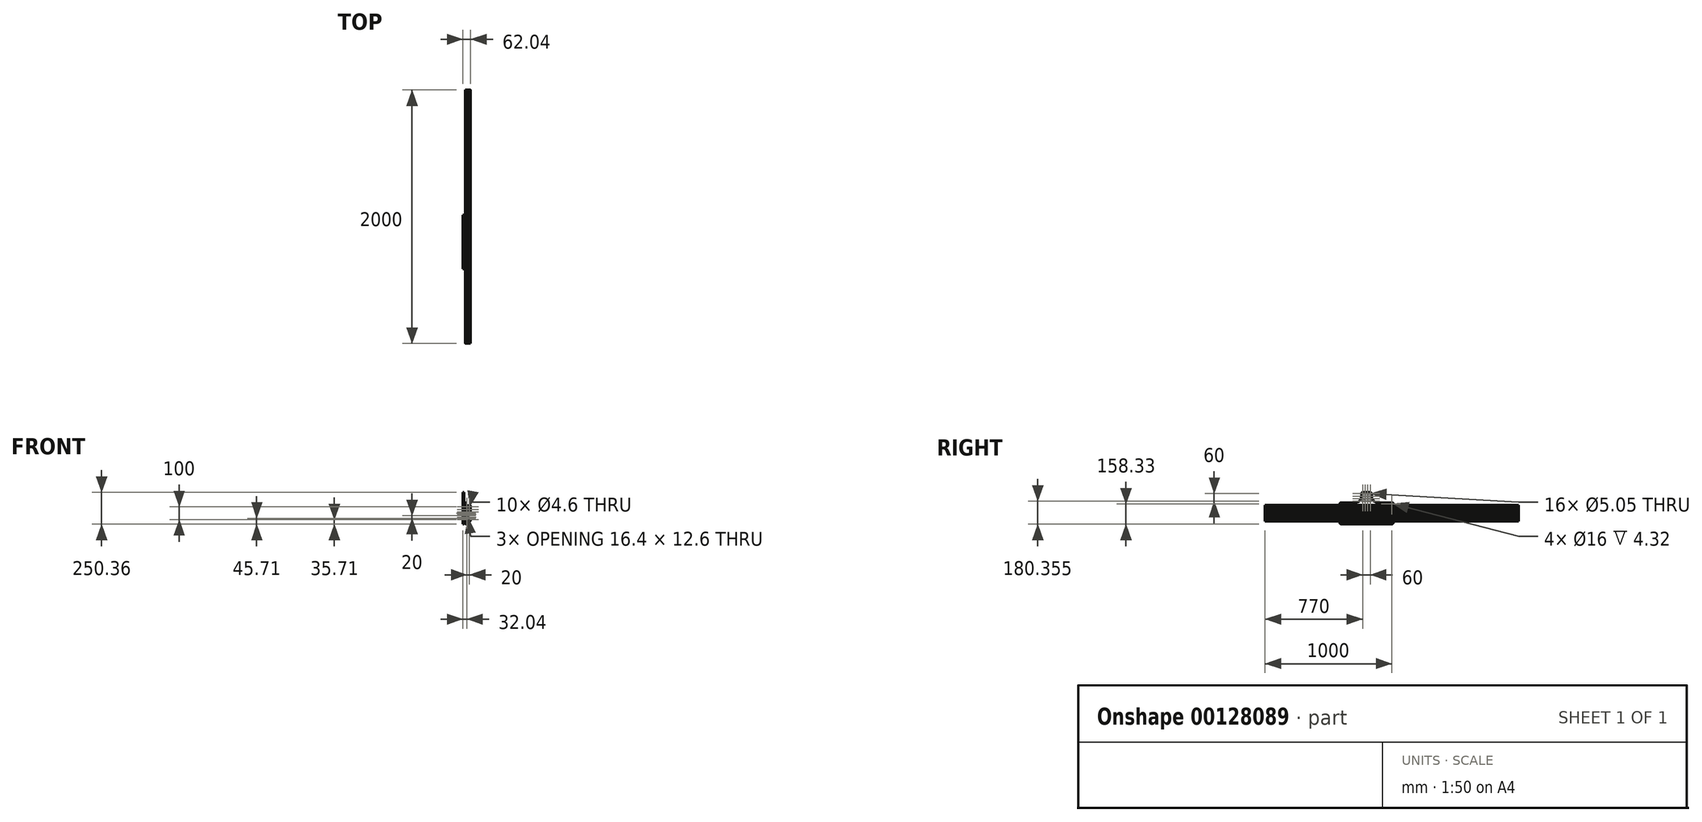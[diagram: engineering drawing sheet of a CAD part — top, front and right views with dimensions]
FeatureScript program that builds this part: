
annotation { "Feature Type Name" : "Feature", "Feature Type Description" : "" }
export const myFeature = defineFeature(function(context is Context, id is Id, definition is map)
    precondition{}
    {
        {
            var Q0;
            Q0=qCreatedBy(makeId("Front.planeOp"),FACE);
            var sketch = newSketch(context, id + "F0", { "sketchPlane" : qUnion([Q0])});
            skLineSegment(sketch, "E0", {"start": v(2.7, -58.2) * mm, "end": v(2.7, -56.24) * mm});
            skLineSegment(sketch, "E1", {"start": v(2.7, -56.24) * mm, "end": v(6.1, -52.84) * mm});
            skLineSegment(sketch, "E2", {"start": v(-1.8, -37.3) * mm, "end": v(-3.79, -37.27) * mm});
            skLineSegment(sketch, "E3", {"start": v(-3.79, -37.27) * mm, "end": v(-7.16, -33.9) * mm});
            skLineSegment(sketch, "E4", {"start": v(-7.16, -33.9) * mm, "end": v(-9.8, -33.9) * mm});
            skLineSegment(sketch, "E5", {"start": v(-9.8, -33.9) * mm, "end": v(-10, -33.7) * mm});
            skLineSegment(sketch, "E6", {"start": v(-10, -33.7) * mm, "end": v(-10.2, -33.9) * mm});
            skLineSegment(sketch, "E7", {"start": v(-10.2, -33.9) * mm, "end": v(-12.84, -33.9) * mm});
            skLineSegment(sketch, "E8", {"start": v(-12.84, -33.9) * mm, "end": v(-16.21, -37.27) * mm});
            skLineSegment(sketch, "E9", {"start": v(-16.21, -37.27) * mm, "end": v(-18.2, -37.3) * mm});
            skLineSegment(sketch, "E10", {"start": v(-18.2, -37.3) * mm, "end": v(-18.2, -40) * mm});
            skLineSegment(sketch, "E11", {"start": v(-18.2, -40) * mm, "end": v(-18.2, -42.7) * mm});
            skLineSegment(sketch, "E12", {"start": v(-18.2, -42.7) * mm, "end": v(-16.21, -42.73) * mm});
            skLineSegment(sketch, "E13", {"start": v(-16.21, -42.73) * mm, "end": v(-12.84, -46.1) * mm});
            skLineSegment(sketch, "E14", {"start": v(-12.84, -46.1) * mm, "end": v(-10.2, -46.1) * mm});
            skLineSegment(sketch, "E15", {"start": v(-10.2, -46.1) * mm, "end": v(-10, -46.3) * mm});
            skLineSegment(sketch, "E16", {"start": v(-10, -46.3) * mm, "end": v(-9.8, -46.1) * mm});
            skLineSegment(sketch, "E17", {"start": v(-9.8, -46.1) * mm, "end": v(-7.16, -46.1) * mm});
            skLineSegment(sketch, "E18", {"start": v(-7.16, -46.1) * mm, "end": v(-1.8, -40.74) * mm});
            skLineSegment(sketch, "E19", {"start": v(-1.8, -40.74) * mm, "end": v(-1.8, -37.3) * mm});
            skLineSegment(sketch, "E20", {"start": v(-6.1, -47.16) * mm, "end": v(-6.1, -49.8) * mm});
            skLineSegment(sketch, "E21", {"start": v(-6.1, -50.2) * mm, "end": v(-6.1, -52.84) * mm});
            skLineSegment(sketch, "E22", {"start": v(-6.1, -52.84) * mm, "end": v(-2.7, -56.24) * mm});
            skLineSegment(sketch, "E23", {"start": v(-2.7, -56.24) * mm, "end": v(-2.7, -58.2) * mm});
            skLineSegment(sketch, "E24", {"start": v(-2.7, -58.2) * mm, "end": v(0, -58.2) * mm});
            skLineSegment(sketch, "E25", {"start": v(0, -58.2) * mm, "end": v(2.7, -58.2) * mm});
            skCircle(sketch, "E26", {"center": v(-10, -50) * mm, "radius": 2.3 * mm});
            skCircle(sketch, "E27", {"center": v(10, -50) * mm, "radius": 2.3 * mm});
            skLineSegment(sketch, "E28", {"start": v(-6.1, -47.16) * mm, "end": v(-0.74, -41.8) * mm});
            skLineSegment(sketch, "E29", {"start": v(-0.74, -41.8) * mm, "end": v(2.7, -41.8) * mm});
            skLineSegment(sketch, "E30", {"start": v(2.7, -41.8) * mm, "end": v(2.7, -43.76) * mm});
            skLineSegment(sketch, "E31", {"start": v(2.7, -43.76) * mm, "end": v(6.1, -47.16) * mm});
            skLineSegment(sketch, "E32", {"start": v(6.1, -47.16) * mm, "end": v(6.1, -49.8) * mm});
            skLineSegment(sketch, "E33", {"start": v(6.1, -49.8) * mm, "end": v(6.3, -50) * mm});
            skLineSegment(sketch, "E34", {"start": v(6.3, -50) * mm, "end": v(6.1, -50.2) * mm});
            skLineSegment(sketch, "E35", {"start": v(6.1, -50.2) * mm, "end": v(6.1, -52.84) * mm});
            skLineSegment(sketch, "E36", {"start": v(-6.1, -50.2) * mm, "end": v(-6.3, -50) * mm});
            skLineSegment(sketch, "E37", {"start": v(-6.3, -50) * mm, "end": v(-6.1, -49.8) * mm});
            skCircle(sketch, "E38", {"center": v(-10, -30) * mm, "radius": 2.3 * mm});
            skLineSegment(sketch, "E39", {"start": v(-3.79, -17.27) * mm, "end": v(-1.8, -17.3) * mm});
            skLineSegment(sketch, "E40", {"start": v(-1.8, -17.3) * mm, "end": v(-1.8, -22.7) * mm});
            skLineSegment(sketch, "E41", {"start": v(-1.8, -22.7) * mm, "end": v(-3.79, -22.73) * mm});
            skLineSegment(sketch, "E42", {"start": v(-3.79, -22.73) * mm, "end": v(-7.16, -26.1) * mm});
            skLineSegment(sketch, "E43", {"start": v(-7.16, -26.1) * mm, "end": v(-9.8, -26.1) * mm});
            skLineSegment(sketch, "E44", {"start": v(-9.8, -26.1) * mm, "end": v(-10, -26.3) * mm});
            skLineSegment(sketch, "E45", {"start": v(-10, -26.3) * mm, "end": v(-10.2, -26.1) * mm});
            skLineSegment(sketch, "E46", {"start": v(-10.2, -26.1) * mm, "end": v(-12.84, -26.1) * mm});
            skLineSegment(sketch, "E47", {"start": v(-12.84, -26.1) * mm, "end": v(-16.21, -22.73) * mm});
            skLineSegment(sketch, "E48", {"start": v(-16.21, -22.73) * mm, "end": v(-18.2, -22.7) * mm});
            skLineSegment(sketch, "E49", {"start": v(-18.2, -22.7) * mm, "end": v(-18.2, -20) * mm});
            skLineSegment(sketch, "E50", {"start": v(-18.2, -20) * mm, "end": v(-18.2, -17.3) * mm});
            skLineSegment(sketch, "E51", {"start": v(-18.2, -17.3) * mm, "end": v(-16.21, -17.27) * mm});
            skLineSegment(sketch, "E52", {"start": v(-16.21, -17.27) * mm, "end": v(-12.84, -13.9) * mm});
            skLineSegment(sketch, "E53", {"start": v(-12.84, -13.9) * mm, "end": v(-10.2, -13.9) * mm});
            skLineSegment(sketch, "E54", {"start": v(-10.2, -13.9) * mm, "end": v(-10, -13.7) * mm});
            skLineSegment(sketch, "E55", {"start": v(-10, -13.7) * mm, "end": v(-9.8, -13.9) * mm});
            skLineSegment(sketch, "E56", {"start": v(-9.8, -13.9) * mm, "end": v(-7.16, -13.9) * mm});
            skLineSegment(sketch, "E57", {"start": v(-7.16, -13.9) * mm, "end": v(-3.79, -17.27) * mm});
            skLineSegment(sketch, "E58", {"start": v(-6.1, -32.84) * mm, "end": v(-6.1, -30.2) * mm});
            skLineSegment(sketch, "E59", {"start": v(-6.1, -30.2) * mm, "end": v(-6.3, -30) * mm});
            skLineSegment(sketch, "E60", {"start": v(-6.3, -30) * mm, "end": v(-6.1, -29.8) * mm});
            skLineSegment(sketch, "E61", {"start": v(-6.1, -29.8) * mm, "end": v(-6.1, -27.16) * mm});
            skLineSegment(sketch, "E62", {"start": v(-6.1, -27.16) * mm, "end": v(-3.44, -24.5) * mm});
            skLineSegment(sketch, "E63", {"start": v(-3.44, -24.5) * mm, "end": v(-1.8, -24.5) * mm});
            skLineSegment(sketch, "E64", {"start": v(-1.8, -24.5) * mm, "end": v(-1.8, -26.61) * mm});
            skLineSegment(sketch, "E65", {"start": v(-1.8, -26.61) * mm, "end": v(-1.2, -26.61) * mm});
            skLineSegment(sketch, "E66", {"start": v(-1.2, -26.61) * mm, "end": v(-0.18, -25.6) * mm});
            skArc(sketch, "E67", {"start": v(-0.18, -25.6) * mm, "mid": v(-0.05, -25.4) * mm, "end": v(0, -25.17) * mm});
            skLineSegment(sketch, "E68", {"start": v(0, -25.17) * mm, "end": v(0, -20.2) * mm});
            skLineSegment(sketch, "E69", {"start": v(0, -20.2) * mm, "end": v(-0.2, -20) * mm});
            skLineSegment(sketch, "E70", {"start": v(-0.2, -20) * mm, "end": v(0, -19.8) * mm});
            skLineSegment(sketch, "E71", {"start": v(0, -19.8) * mm, "end": v(0, -14.83) * mm});
            skArc(sketch, "E72", {"start": v(0, -14.83) * mm, "mid": v(-0.05, -14.6) * mm, "end": v(-0.18, -14.4) * mm});
            skLineSegment(sketch, "E73", {"start": v(-0.18, -14.4) * mm, "end": v(-1.2, -13.39) * mm});
            skLineSegment(sketch, "E74", {"start": v(-1.2, -13.39) * mm, "end": v(-1.8, -13.39) * mm});
            skLineSegment(sketch, "E75", {"start": v(-1.8, -13.39) * mm, "end": v(-1.8, -15.5) * mm});
            skLineSegment(sketch, "E76", {"start": v(-1.8, -15.5) * mm, "end": v(-3.44, -15.5) * mm});
            skLineSegment(sketch, "E77", {"start": v(-3.44, -15.5) * mm, "end": v(-6.1, -12.84) * mm});
            skLineSegment(sketch, "E78", {"start": v(-6.1, -12.84) * mm, "end": v(-6.1, -10.2) * mm});
            skLineSegment(sketch, "E79", {"start": v(-6.1, -10.2) * mm, "end": v(-6.3, -10) * mm});
            skLineSegment(sketch, "E80", {"start": v(-6.3, -10) * mm, "end": v(-6.1, -9.8) * mm});
            skLineSegment(sketch, "E81", {"start": v(-6.1, -9.8) * mm, "end": v(-6.1, -7.16) * mm});
            skLineSegment(sketch, "E82", {"start": v(-6.1, -7.16) * mm, "end": v(-3.44, -4.5) * mm});
            skLineSegment(sketch, "E83", {"start": v(-3.44, -4.5) * mm, "end": v(-1.8, -4.5) * mm});
            skLineSegment(sketch, "E84", {"start": v(-1.8, -4.5) * mm, "end": v(-1.8, -6.61) * mm});
            skLineSegment(sketch, "E85", {"start": v(-1.8, -6.61) * mm, "end": v(-1.2, -6.61) * mm});
            skLineSegment(sketch, "E86", {"start": v(-1.2, -6.61) * mm, "end": v(-0.18, -5.6) * mm});
            skArc(sketch, "E87", {"start": v(-0.18, -5.6) * mm, "mid": v(-0.05, -5.4) * mm, "end": v(0, -5.17) * mm});
            skLineSegment(sketch, "E88", {"start": v(0, -5.17) * mm, "end": v(0, 0) * mm});
            skLineSegment(sketch, "E89", {"start": v(0, 0) * mm, "end": v(5.17, 0) * mm});
            skArc(sketch, "E90", {"start": v(5.17, 0) * mm, "mid": v(5.4, 0.05) * mm, "end": v(5.6, 0.18) * mm});
            skLineSegment(sketch, "E91", {"start": v(5.6, 0.18) * mm, "end": v(6.61, 1.2) * mm});
            skLineSegment(sketch, "E92", {"start": v(6.61, 1.2) * mm, "end": v(6.61, 1.8) * mm});
            skLineSegment(sketch, "E93", {"start": v(6.61, 1.8) * mm, "end": v(4.5, 1.8) * mm});
            skLineSegment(sketch, "E94", {"start": v(4.5, 1.8) * mm, "end": v(4.5, 3.44) * mm});
            skLineSegment(sketch, "E95", {"start": v(4.5, 3.44) * mm, "end": v(7.16, 6.1) * mm});
            skLineSegment(sketch, "E96", {"start": v(7.16, 6.1) * mm, "end": v(9.8, 6.1) * mm});
            skLineSegment(sketch, "E97", {"start": v(9.8, 6.1) * mm, "end": v(10, 6.3) * mm});
            skLineSegment(sketch, "E98", {"start": v(10, 6.3) * mm, "end": v(10.2, 6.1) * mm});
            skLineSegment(sketch, "E99", {"start": v(10.2, 6.1) * mm, "end": v(12.84, 6.1) * mm});
            skLineSegment(sketch, "E100", {"start": v(12.84, 6.1) * mm, "end": v(15.5, 3.44) * mm});
            skLineSegment(sketch, "E101", {"start": v(15.5, 3.44) * mm, "end": v(15.5, 1.8) * mm});
            skLineSegment(sketch, "E102", {"start": v(15.5, 1.8) * mm, "end": v(13.39, 1.8) * mm});
            skLineSegment(sketch, "E103", {"start": v(13.39, 1.8) * mm, "end": v(13.39, 1.2) * mm});
            skLineSegment(sketch, "E104", {"start": v(13.39, 1.2) * mm, "end": v(14.4, 0.18) * mm});
            skArc(sketch, "E105", {"start": v(14.4, 0.18) * mm, "mid": v(14.6, 0.05) * mm, "end": v(14.83, 0) * mm});
            skLineSegment(sketch, "E106", {"start": v(14.83, 0) * mm, "end": v(18.5, 0) * mm});
            skArc(sketch, "E107", {"start": v(18.5, 0) * mm, "mid": v(19.56, 0.44) * mm, "end": v(20, 1.5) * mm});
            skLineSegment(sketch, "E108", {"start": v(20, 1.5) * mm, "end": v(20, 5.17) * mm});
            skArc(sketch, "E109", {"start": v(20, 5.17) * mm, "mid": v(19.95, 5.4) * mm, "end": v(19.82, 5.6) * mm});
            skLineSegment(sketch, "E110", {"start": v(19.82, 5.6) * mm, "end": v(18.8, 6.61) * mm});
            skLineSegment(sketch, "E111", {"start": v(18.8, 6.61) * mm, "end": v(18.2, 6.61) * mm});
            skLineSegment(sketch, "E112", {"start": v(18.2, 6.61) * mm, "end": v(18.2, 4.5) * mm});
            skLineSegment(sketch, "E113", {"start": v(18.2, 4.5) * mm, "end": v(16.56, 4.5) * mm});
            skLineSegment(sketch, "E114", {"start": v(16.56, 4.5) * mm, "end": v(13.9, 7.16) * mm});
            skLineSegment(sketch, "E115", {"start": v(13.9, 7.16) * mm, "end": v(13.9, 9.8) * mm});
            skLineSegment(sketch, "E116", {"start": v(13.9, 9.8) * mm, "end": v(13.7, 10) * mm});
            skLineSegment(sketch, "E117", {"start": v(13.7, 10) * mm, "end": v(13.9, 10.2) * mm});
            skLineSegment(sketch, "E118", {"start": v(13.9, 10.2) * mm, "end": v(13.9, 12.84) * mm});
            skLineSegment(sketch, "E119", {"start": v(13.9, 12.84) * mm, "end": v(16.56, 15.5) * mm});
            skLineSegment(sketch, "E120", {"start": v(16.56, 15.5) * mm, "end": v(18.2, 15.5) * mm});
            skLineSegment(sketch, "E121", {"start": v(18.2, 15.5) * mm, "end": v(18.2, 13.39) * mm});
            skLineSegment(sketch, "E122", {"start": v(18.2, 13.39) * mm, "end": v(18.8, 13.39) * mm});
            skLineSegment(sketch, "E123", {"start": v(18.8, 13.39) * mm, "end": v(19.82, 14.4) * mm});
            skArc(sketch, "E124", {"start": v(19.82, 14.4) * mm, "mid": v(19.95, 14.6) * mm, "end": v(20, 14.83) * mm});
            skLineSegment(sketch, "E125", {"start": v(20, 14.83) * mm, "end": v(20, 18.5) * mm});
            skArc(sketch, "E126", {"start": v(20, 18.5) * mm, "mid": v(19.56, 19.56) * mm, "end": v(18.5, 20) * mm});
            skLineSegment(sketch, "E127", {"start": v(18.5, 20) * mm, "end": v(14.83, 20) * mm});
            skArc(sketch, "E128", {"start": v(14.83, 20) * mm, "mid": v(14.6, 19.95) * mm, "end": v(14.4, 19.82) * mm});
            skLineSegment(sketch, "E129", {"start": v(14.4, 19.82) * mm, "end": v(13.39, 18.8) * mm});
            skLineSegment(sketch, "E130", {"start": v(13.39, 18.8) * mm, "end": v(13.39, 18.2) * mm});
            skLineSegment(sketch, "E131", {"start": v(13.39, 18.2) * mm, "end": v(15.5, 18.2) * mm});
            skLineSegment(sketch, "E132", {"start": v(15.5, 18.2) * mm, "end": v(15.5, 16.56) * mm});
            skLineSegment(sketch, "E133", {"start": v(15.5, 16.56) * mm, "end": v(12.84, 13.9) * mm});
            skLineSegment(sketch, "E134", {"start": v(12.84, 13.9) * mm, "end": v(10.2, 13.9) * mm});
            skLineSegment(sketch, "E135", {"start": v(10.2, 13.9) * mm, "end": v(10, 13.7) * mm});
            skLineSegment(sketch, "E136", {"start": v(10, 13.7) * mm, "end": v(9.8, 13.9) * mm});
            skLineSegment(sketch, "E137", {"start": v(9.8, 13.9) * mm, "end": v(7.16, 13.9) * mm});
            skLineSegment(sketch, "E138", {"start": v(7.16, 13.9) * mm, "end": v(4.5, 16.56) * mm});
            skLineSegment(sketch, "E139", {"start": v(4.5, 16.56) * mm, "end": v(4.5, 18.2) * mm});
            skLineSegment(sketch, "E140", {"start": v(4.5, 18.2) * mm, "end": v(6.61, 18.2) * mm});
            skLineSegment(sketch, "E141", {"start": v(6.61, 18.2) * mm, "end": v(6.61, 18.8) * mm});
            skLineSegment(sketch, "E142", {"start": v(6.61, 18.8) * mm, "end": v(5.6, 19.82) * mm});
            skArc(sketch, "E143", {"start": v(5.6, 19.82) * mm, "mid": v(5.4, 19.95) * mm, "end": v(5.17, 20) * mm});
            skLineSegment(sketch, "E144", {"start": v(5.17, 20) * mm, "end": v(0.2, 20) * mm});
            skLineSegment(sketch, "E145", {"start": v(0.2, 20) * mm, "end": v(0, 19.8) * mm});
            skLineSegment(sketch, "E146", {"start": v(0, 19.8) * mm, "end": v(-0.2, 20) * mm});
            skLineSegment(sketch, "E147", {"start": v(-0.2, 20) * mm, "end": v(-5.17, 20) * mm});
            skArc(sketch, "E148", {"start": v(-5.17, 20) * mm, "mid": v(-5.4, 19.95) * mm, "end": v(-5.6, 19.82) * mm});
            skLineSegment(sketch, "E149", {"start": v(-5.6, 19.82) * mm, "end": v(-6.61, 18.8) * mm});
            skLineSegment(sketch, "E150", {"start": v(-6.61, 18.8) * mm, "end": v(-6.61, 18.2) * mm});
            skLineSegment(sketch, "E151", {"start": v(-6.61, 18.2) * mm, "end": v(-4.5, 18.2) * mm});
            skLineSegment(sketch, "E152", {"start": v(-4.5, 18.2) * mm, "end": v(-4.5, 16.56) * mm});
            skLineSegment(sketch, "E153", {"start": v(-4.5, 16.56) * mm, "end": v(-7.16, 13.9) * mm});
            skLineSegment(sketch, "E154", {"start": v(-7.16, 13.9) * mm, "end": v(-9.8, 13.9) * mm});
            skLineSegment(sketch, "E155", {"start": v(-9.8, 13.9) * mm, "end": v(-10, 13.7) * mm});
            skLineSegment(sketch, "E156", {"start": v(-10, 13.7) * mm, "end": v(-10.2, 13.9) * mm});
            skLineSegment(sketch, "E157", {"start": v(-10.2, 13.9) * mm, "end": v(-12.84, 13.9) * mm});
            skLineSegment(sketch, "E158", {"start": v(-12.84, 13.9) * mm, "end": v(-15.5, 16.56) * mm});
            skLineSegment(sketch, "E159", {"start": v(-15.5, 16.56) * mm, "end": v(-15.5, 18.2) * mm});
            skLineSegment(sketch, "E160", {"start": v(-15.5, 18.2) * mm, "end": v(-13.39, 18.2) * mm});
            skLineSegment(sketch, "E161", {"start": v(-13.39, 18.2) * mm, "end": v(-13.39, 18.8) * mm});
            skLineSegment(sketch, "E162", {"start": v(-13.39, 18.8) * mm, "end": v(-14.4, 19.82) * mm});
            skArc(sketch, "E163", {"start": v(-14.4, 19.82) * mm, "mid": v(-14.6, 19.95) * mm, "end": v(-14.83, 20) * mm});
            skLineSegment(sketch, "E164", {"start": v(-14.83, 20) * mm, "end": v(-18.5, 20) * mm});
            skArc(sketch, "E165", {"start": v(-18.5, 20) * mm, "mid": v(-19.56, 19.56) * mm, "end": v(-20, 18.5) * mm});
            skLineSegment(sketch, "E166", {"start": v(-20, 18.5) * mm, "end": v(-20, 14.83) * mm});
            skArc(sketch, "E167", {"start": v(-20, 14.83) * mm, "mid": v(-19.95, 14.6) * mm, "end": v(-19.82, 14.4) * mm});
            skLineSegment(sketch, "E168", {"start": v(-19.82, 14.4) * mm, "end": v(-18.8, 13.39) * mm});
            skLineSegment(sketch, "E169", {"start": v(-18.8, 13.39) * mm, "end": v(-18.2, 13.39) * mm});
            skLineSegment(sketch, "E170", {"start": v(-18.2, 13.39) * mm, "end": v(-18.2, 15.5) * mm});
            skLineSegment(sketch, "E171", {"start": v(-18.2, 15.5) * mm, "end": v(-16.56, 15.5) * mm});
            skLineSegment(sketch, "E172", {"start": v(-16.56, 15.5) * mm, "end": v(-13.9, 12.84) * mm});
            skLineSegment(sketch, "E173", {"start": v(-13.9, 12.84) * mm, "end": v(-13.9, 10.2) * mm});
            skLineSegment(sketch, "E174", {"start": v(-13.9, 10.2) * mm, "end": v(-13.7, 10) * mm});
            skLineSegment(sketch, "E175", {"start": v(-13.7, 10) * mm, "end": v(-13.9, 9.8) * mm});
            skLineSegment(sketch, "E176", {"start": v(-13.9, 9.8) * mm, "end": v(-13.9, 7.16) * mm});
            skLineSegment(sketch, "E177", {"start": v(-13.9, 7.16) * mm, "end": v(-16.56, 4.5) * mm});
            skLineSegment(sketch, "E178", {"start": v(-16.56, 4.5) * mm, "end": v(-18.2, 4.5) * mm});
            skLineSegment(sketch, "E179", {"start": v(-18.2, 4.5) * mm, "end": v(-18.2, 6.61) * mm});
            skLineSegment(sketch, "E180", {"start": v(-18.2, 6.61) * mm, "end": v(-18.8, 6.61) * mm});
            skLineSegment(sketch, "E181", {"start": v(-18.8, 6.61) * mm, "end": v(-19.82, 5.6) * mm});
            skArc(sketch, "E182", {"start": v(-19.82, 5.6) * mm, "mid": v(-19.95, 5.4) * mm, "end": v(-20, 5.17) * mm});
            skLineSegment(sketch, "E183", {"start": v(-20, 5.17) * mm, "end": v(-20, 0.2) * mm});
            skLineSegment(sketch, "E184", {"start": v(-20, 0.2) * mm, "end": v(-19.8, 0) * mm});
            skLineSegment(sketch, "E185", {"start": v(-19.8, 0) * mm, "end": v(-20, -0.2) * mm});
            skLineSegment(sketch, "E186", {"start": v(-20, -0.2) * mm, "end": v(-20, -5.17) * mm});
            skArc(sketch, "E187", {"start": v(-20, -5.17) * mm, "mid": v(-19.95, -5.4) * mm, "end": v(-19.82, -5.6) * mm});
            skLineSegment(sketch, "E188", {"start": v(-19.82, -5.6) * mm, "end": v(-18.8, -6.61) * mm});
            skLineSegment(sketch, "E189", {"start": v(-18.8, -6.61) * mm, "end": v(-18.2, -6.61) * mm});
            skLineSegment(sketch, "E190", {"start": v(-18.2, -6.61) * mm, "end": v(-18.2, -4.5) * mm});
            skLineSegment(sketch, "E191", {"start": v(-18.2, -4.5) * mm, "end": v(-16.56, -4.5) * mm});
            skLineSegment(sketch, "E192", {"start": v(-16.56, -4.5) * mm, "end": v(-13.9, -7.16) * mm});
            skLineSegment(sketch, "E193", {"start": v(-13.9, -7.16) * mm, "end": v(-13.9, -9.8) * mm});
            skLineSegment(sketch, "E194", {"start": v(-13.9, -9.8) * mm, "end": v(-13.7, -10) * mm});
            skLineSegment(sketch, "E195", {"start": v(-13.7, -10) * mm, "end": v(-13.9, -10.2) * mm});
            skLineSegment(sketch, "E196", {"start": v(-13.9, -10.2) * mm, "end": v(-13.9, -12.84) * mm});
            skLineSegment(sketch, "E197", {"start": v(-13.9, -12.84) * mm, "end": v(-16.56, -15.5) * mm});
            skLineSegment(sketch, "E198", {"start": v(-16.56, -15.5) * mm, "end": v(-18.2, -15.5) * mm});
            skLineSegment(sketch, "E199", {"start": v(-18.2, -15.5) * mm, "end": v(-18.2, -13.39) * mm});
            skLineSegment(sketch, "E200", {"start": v(-18.2, -13.39) * mm, "end": v(-18.8, -13.39) * mm});
            skLineSegment(sketch, "E201", {"start": v(-18.8, -13.39) * mm, "end": v(-19.82, -14.4) * mm});
            skArc(sketch, "E202", {"start": v(-19.82, -14.4) * mm, "mid": v(-19.95, -14.6) * mm, "end": v(-20, -14.83) * mm});
            skLineSegment(sketch, "E203", {"start": v(-20, -14.83) * mm, "end": v(-20, -19.8) * mm});
            skLineSegment(sketch, "E204", {"start": v(-20, -19.8) * mm, "end": v(-19.8, -20) * mm});
            skLineSegment(sketch, "E205", {"start": v(-19.8, -20) * mm, "end": v(-20, -20.2) * mm});
            skLineSegment(sketch, "E206", {"start": v(-20, -20.2) * mm, "end": v(-20, -25.17) * mm});
            skArc(sketch, "E207", {"start": v(-20, -25.17) * mm, "mid": v(-19.95, -25.4) * mm, "end": v(-19.82, -25.6) * mm});
            skLineSegment(sketch, "E208", {"start": v(-19.82, -25.6) * mm, "end": v(-18.8, -26.61) * mm});
            skLineSegment(sketch, "E209", {"start": v(-18.8, -26.61) * mm, "end": v(-18.2, -26.61) * mm});
            skLineSegment(sketch, "E210", {"start": v(-18.2, -26.61) * mm, "end": v(-18.2, -24.5) * mm});
            skLineSegment(sketch, "E211", {"start": v(-18.2, -24.5) * mm, "end": v(-16.56, -24.5) * mm});
            skLineSegment(sketch, "E212", {"start": v(-16.56, -24.5) * mm, "end": v(-13.9, -27.16) * mm});
            skLineSegment(sketch, "E213", {"start": v(-13.9, -27.16) * mm, "end": v(-13.9, -29.8) * mm});
            skLineSegment(sketch, "E214", {"start": v(-13.9, -29.8) * mm, "end": v(-13.7, -30) * mm});
            skLineSegment(sketch, "E215", {"start": v(-13.7, -30) * mm, "end": v(-13.9, -30.2) * mm});
            skLineSegment(sketch, "E216", {"start": v(-13.9, -30.2) * mm, "end": v(-13.9, -32.84) * mm});
            skLineSegment(sketch, "E217", {"start": v(-13.9, -32.84) * mm, "end": v(-16.56, -35.5) * mm});
            skLineSegment(sketch, "E218", {"start": v(-16.56, -35.5) * mm, "end": v(-18.2, -35.5) * mm});
            skLineSegment(sketch, "E219", {"start": v(-18.2, -35.5) * mm, "end": v(-18.2, -33.39) * mm});
            skLineSegment(sketch, "E220", {"start": v(-18.2, -33.39) * mm, "end": v(-18.8, -33.39) * mm});
            skLineSegment(sketch, "E221", {"start": v(-18.8, -33.39) * mm, "end": v(-19.82, -34.4) * mm});
            skArc(sketch, "E222", {"start": v(-19.82, -34.4) * mm, "mid": v(-19.95, -34.6) * mm, "end": v(-20, -34.83) * mm});
            skLineSegment(sketch, "E223", {"start": v(-20, -34.83) * mm, "end": v(-20, -39.8) * mm});
            skLineSegment(sketch, "E224", {"start": v(-20, -39.8) * mm, "end": v(-19.8, -40) * mm});
            skLineSegment(sketch, "E225", {"start": v(-19.8, -40) * mm, "end": v(-20, -40.2) * mm});
            skLineSegment(sketch, "E226", {"start": v(-20, -40.2) * mm, "end": v(-20, -45.17) * mm});
            skArc(sketch, "E227", {"start": v(-20, -45.17) * mm, "mid": v(-19.95, -45.4) * mm, "end": v(-19.82, -45.6) * mm});
            skLineSegment(sketch, "E228", {"start": v(-19.82, -45.6) * mm, "end": v(-18.8, -46.61) * mm});
            skLineSegment(sketch, "E229", {"start": v(-18.8, -46.61) * mm, "end": v(-18.2, -46.61) * mm});
            skLineSegment(sketch, "E230", {"start": v(-18.2, -46.61) * mm, "end": v(-18.2, -44.5) * mm});
            skLineSegment(sketch, "E231", {"start": v(-18.2, -44.5) * mm, "end": v(-16.56, -44.5) * mm});
            skLineSegment(sketch, "E232", {"start": v(-16.56, -44.5) * mm, "end": v(-13.9, -47.16) * mm});
            skLineSegment(sketch, "E233", {"start": v(-13.9, -47.16) * mm, "end": v(-13.9, -49.8) * mm});
            skLineSegment(sketch, "E234", {"start": v(-13.9, -49.8) * mm, "end": v(-13.7, -50) * mm});
            skLineSegment(sketch, "E235", {"start": v(-13.7, -50) * mm, "end": v(-13.9, -50.2) * mm});
            skLineSegment(sketch, "E236", {"start": v(-13.9, -50.2) * mm, "end": v(-13.9, -52.84) * mm});
            skLineSegment(sketch, "E237", {"start": v(-13.9, -52.84) * mm, "end": v(-16.56, -55.5) * mm});
            skLineSegment(sketch, "E238", {"start": v(-16.56, -55.5) * mm, "end": v(-18.2, -55.5) * mm});
            skLineSegment(sketch, "E239", {"start": v(-18.2, -55.5) * mm, "end": v(-18.2, -53.39) * mm});
            skLineSegment(sketch, "E240", {"start": v(-18.2, -53.39) * mm, "end": v(-18.8, -53.39) * mm});
            skLineSegment(sketch, "E241", {"start": v(-18.8, -53.39) * mm, "end": v(-19.82, -54.4) * mm});
            skArc(sketch, "E242", {"start": v(-19.82, -54.4) * mm, "mid": v(-19.95, -54.6) * mm, "end": v(-20, -54.83) * mm});
            skLineSegment(sketch, "E243", {"start": v(-20, -54.83) * mm, "end": v(-20, -58.5) * mm});
            skArc(sketch, "E244", {"start": v(-20, -58.5) * mm, "mid": v(-19.56, -59.56) * mm, "end": v(-18.5, -60) * mm});
            skLineSegment(sketch, "E245", {"start": v(-18.5, -60) * mm, "end": v(-14.83, -60) * mm});
            skArc(sketch, "E246", {"start": v(-14.83, -60) * mm, "mid": v(-14.6, -59.95) * mm, "end": v(-14.4, -59.82) * mm});
            skLineSegment(sketch, "E247", {"start": v(-14.4, -59.82) * mm, "end": v(-13.39, -58.8) * mm});
            skLineSegment(sketch, "E248", {"start": v(-13.39, -58.8) * mm, "end": v(-13.39, -58.2) * mm});
            skLineSegment(sketch, "E249", {"start": v(-13.39, -58.2) * mm, "end": v(-15.5, -58.2) * mm});
            skLineSegment(sketch, "E250", {"start": v(-15.5, -58.2) * mm, "end": v(-15.5, -56.56) * mm});
            skLineSegment(sketch, "E251", {"start": v(-15.5, -56.56) * mm, "end": v(-12.84, -53.9) * mm});
            skLineSegment(sketch, "E252", {"start": v(-12.84, -53.9) * mm, "end": v(-10.2, -53.9) * mm});
            skLineSegment(sketch, "E253", {"start": v(-10.2, -53.9) * mm, "end": v(-10, -53.7) * mm});
            skLineSegment(sketch, "E254", {"start": v(-10, -53.7) * mm, "end": v(-9.8, -53.9) * mm});
            skLineSegment(sketch, "E255", {"start": v(-9.8, -53.9) * mm, "end": v(-7.16, -53.9) * mm});
            skLineSegment(sketch, "E256", {"start": v(-7.16, -53.9) * mm, "end": v(-4.5, -56.56) * mm});
            skLineSegment(sketch, "E257", {"start": v(-4.5, -56.56) * mm, "end": v(-4.5, -58.2) * mm});
            skLineSegment(sketch, "E258", {"start": v(-4.5, -58.2) * mm, "end": v(-6.61, -58.2) * mm});
            skLineSegment(sketch, "E259", {"start": v(-6.61, -58.2) * mm, "end": v(-6.61, -58.8) * mm});
            skLineSegment(sketch, "E260", {"start": v(-6.61, -58.8) * mm, "end": v(-5.6, -59.82) * mm});
            skArc(sketch, "E261", {"start": v(-5.6, -59.82) * mm, "mid": v(-5.4, -59.95) * mm, "end": v(-5.17, -60) * mm});
            skLineSegment(sketch, "E262", {"start": v(-5.17, -60) * mm, "end": v(-0.2, -60) * mm});
            skLineSegment(sketch, "E263", {"start": v(-0.2, -60) * mm, "end": v(0, -59.8) * mm});
            skLineSegment(sketch, "E264", {"start": v(0, -59.8) * mm, "end": v(0.2, -60) * mm});
            skLineSegment(sketch, "E265", {"start": v(0.2, -60) * mm, "end": v(5.17, -60) * mm});
            skArc(sketch, "E266", {"start": v(5.17, -60) * mm, "mid": v(5.4, -59.95) * mm, "end": v(5.6, -59.82) * mm});
            skLineSegment(sketch, "E267", {"start": v(5.6, -59.82) * mm, "end": v(6.61, -58.8) * mm});
            skLineSegment(sketch, "E268", {"start": v(6.61, -58.8) * mm, "end": v(6.61, -58.2) * mm});
            skLineSegment(sketch, "E269", {"start": v(6.61, -58.2) * mm, "end": v(4.5, -58.2) * mm});
            skLineSegment(sketch, "E270", {"start": v(4.5, -58.2) * mm, "end": v(4.5, -56.56) * mm});
            skLineSegment(sketch, "E271", {"start": v(4.5, -56.56) * mm, "end": v(7.16, -53.9) * mm});
            skLineSegment(sketch, "E272", {"start": v(7.16, -53.9) * mm, "end": v(9.8, -53.9) * mm});
            skLineSegment(sketch, "E273", {"start": v(9.8, -53.9) * mm, "end": v(10, -53.7) * mm});
            skLineSegment(sketch, "E274", {"start": v(10, -53.7) * mm, "end": v(10.2, -53.9) * mm});
            skLineSegment(sketch, "E275", {"start": v(10.2, -53.9) * mm, "end": v(12.84, -53.9) * mm});
            skLineSegment(sketch, "E276", {"start": v(12.84, -53.9) * mm, "end": v(15.5, -56.56) * mm});
            skLineSegment(sketch, "E277", {"start": v(15.5, -56.56) * mm, "end": v(15.5, -58.2) * mm});
            skLineSegment(sketch, "E278", {"start": v(15.5, -58.2) * mm, "end": v(13.39, -58.2) * mm});
            skLineSegment(sketch, "E279", {"start": v(13.39, -58.2) * mm, "end": v(13.39, -58.8) * mm});
            skLineSegment(sketch, "E280", {"start": v(13.39, -58.8) * mm, "end": v(14.4, -59.82) * mm});
            skArc(sketch, "E281", {"start": v(14.4, -59.82) * mm, "mid": v(14.6, -59.95) * mm, "end": v(14.83, -60) * mm});
            skLineSegment(sketch, "E282", {"start": v(14.83, -60) * mm, "end": v(18.5, -60) * mm});
            skArc(sketch, "E283", {"start": v(18.5, -60) * mm, "mid": v(19.56, -59.56) * mm, "end": v(20, -58.5) * mm});
            skLineSegment(sketch, "E284", {"start": v(20, -58.5) * mm, "end": v(20, -54.83) * mm});
            skArc(sketch, "E285", {"start": v(20, -54.83) * mm, "mid": v(19.95, -54.6) * mm, "end": v(19.82, -54.4) * mm});
            skLineSegment(sketch, "E286", {"start": v(19.82, -54.4) * mm, "end": v(18.8, -53.39) * mm});
            skLineSegment(sketch, "E287", {"start": v(18.8, -53.39) * mm, "end": v(18.2, -53.39) * mm});
            skLineSegment(sketch, "E288", {"start": v(18.2, -53.39) * mm, "end": v(18.2, -55.5) * mm});
            skLineSegment(sketch, "E289", {"start": v(18.2, -55.5) * mm, "end": v(16.56, -55.5) * mm});
            skLineSegment(sketch, "E290", {"start": v(16.56, -55.5) * mm, "end": v(13.9, -52.84) * mm});
            skLineSegment(sketch, "E291", {"start": v(13.9, -52.84) * mm, "end": v(13.9, -50.2) * mm});
            skLineSegment(sketch, "E292", {"start": v(13.9, -50.2) * mm, "end": v(13.7, -50) * mm});
            skLineSegment(sketch, "E293", {"start": v(13.7, -50) * mm, "end": v(13.9, -49.8) * mm});
            skLineSegment(sketch, "E294", {"start": v(13.9, -49.8) * mm, "end": v(13.9, -47.16) * mm});
            skLineSegment(sketch, "E295", {"start": v(13.9, -47.16) * mm, "end": v(16.56, -44.5) * mm});
            skLineSegment(sketch, "E296", {"start": v(16.56, -44.5) * mm, "end": v(18.2, -44.5) * mm});
            skLineSegment(sketch, "E297", {"start": v(18.2, -44.5) * mm, "end": v(18.2, -46.61) * mm});
            skLineSegment(sketch, "E298", {"start": v(18.2, -46.61) * mm, "end": v(18.8, -46.61) * mm});
            skLineSegment(sketch, "E299", {"start": v(18.8, -46.61) * mm, "end": v(19.82, -45.6) * mm});
            skArc(sketch, "E300", {"start": v(19.82, -45.6) * mm, "mid": v(19.95, -45.4) * mm, "end": v(20, -45.17) * mm});
            skLineSegment(sketch, "E301", {"start": v(20, -45.17) * mm, "end": v(20, -41.5) * mm});
            skArc(sketch, "E302", {"start": v(20, -41.5) * mm, "mid": v(19.56, -40.44) * mm, "end": v(18.5, -40) * mm});
            skLineSegment(sketch, "E303", {"start": v(18.5, -40) * mm, "end": v(14.83, -40) * mm});
            skArc(sketch, "E304", {"start": v(14.83, -40) * mm, "mid": v(14.6, -40.05) * mm, "end": v(14.4, -40.18) * mm});
            skLineSegment(sketch, "E305", {"start": v(14.4, -40.18) * mm, "end": v(13.39, -41.2) * mm});
            skLineSegment(sketch, "E306", {"start": v(13.39, -41.2) * mm, "end": v(13.39, -41.8) * mm});
            skLineSegment(sketch, "E307", {"start": v(13.39, -41.8) * mm, "end": v(15.5, -41.8) * mm});
            skLineSegment(sketch, "E308", {"start": v(15.5, -41.8) * mm, "end": v(15.5, -43.44) * mm});
            skLineSegment(sketch, "E309", {"start": v(15.5, -43.44) * mm, "end": v(12.84, -46.1) * mm});
            skLineSegment(sketch, "E310", {"start": v(12.84, -46.1) * mm, "end": v(10.2, -46.1) * mm});
            skLineSegment(sketch, "E311", {"start": v(10.2, -46.1) * mm, "end": v(10, -46.3) * mm});
            skLineSegment(sketch, "E312", {"start": v(10, -46.3) * mm, "end": v(9.8, -46.1) * mm});
            skLineSegment(sketch, "E313", {"start": v(9.8, -46.1) * mm, "end": v(7.16, -46.1) * mm});
            skLineSegment(sketch, "E314", {"start": v(7.16, -46.1) * mm, "end": v(4.5, -43.44) * mm});
            skLineSegment(sketch, "E315", {"start": v(4.5, -43.44) * mm, "end": v(4.5, -41.8) * mm});
            skLineSegment(sketch, "E316", {"start": v(4.5, -41.8) * mm, "end": v(6.61, -41.8) * mm});
            skLineSegment(sketch, "E317", {"start": v(6.61, -41.8) * mm, "end": v(6.61, -41.2) * mm});
            skLineSegment(sketch, "E318", {"start": v(6.61, -41.2) * mm, "end": v(5.6, -40.18) * mm});
            skArc(sketch, "E319", {"start": v(5.6, -40.18) * mm, "mid": v(5.4, -40.05) * mm, "end": v(5.17, -40) * mm});
            skLineSegment(sketch, "E320", {"start": v(5.17, -40) * mm, "end": v(0, -40) * mm});
            skLineSegment(sketch, "E321", {"start": v(0, -40) * mm, "end": v(0, -34.83) * mm});
            skArc(sketch, "E322", {"start": v(0, -34.83) * mm, "mid": v(-0.05, -34.6) * mm, "end": v(-0.18, -34.4) * mm});
            skLineSegment(sketch, "E323", {"start": v(-0.18, -34.4) * mm, "end": v(-1.2, -33.39) * mm});
            skLineSegment(sketch, "E324", {"start": v(-1.2, -33.39) * mm, "end": v(-1.8, -33.39) * mm});
            skLineSegment(sketch, "E325", {"start": v(-1.8, -33.39) * mm, "end": v(-1.8, -35.5) * mm});
            skLineSegment(sketch, "E326", {"start": v(-1.8, -35.5) * mm, "end": v(-3.44, -35.5) * mm});
            skLineSegment(sketch, "E327", {"start": v(-3.44, -35.5) * mm, "end": v(-6.1, -32.84) * mm});
            skLineSegment(sketch, "E328", {"start": v(2.7, 18.2) * mm, "end": v(2.7, 16.24) * mm});
            skLineSegment(sketch, "E329", {"start": v(2.7, 16.24) * mm, "end": v(6.1, 12.84) * mm});
            skLineSegment(sketch, "E330", {"start": v(-12.84, -6.1) * mm, "end": v(-16.21, -2.73) * mm});
            skLineSegment(sketch, "E331", {"start": v(-16.21, -2.73) * mm, "end": v(-18.2, -2.7) * mm});
            skLineSegment(sketch, "E332", {"start": v(-18.2, -2.7) * mm, "end": v(-18.2, 0) * mm});
            skLineSegment(sketch, "E333", {"start": v(-18.2, 0) * mm, "end": v(-18.2, 2.7) * mm});
            skLineSegment(sketch, "E334", {"start": v(-18.2, 2.7) * mm, "end": v(-16.21, 2.73) * mm});
            skLineSegment(sketch, "E335", {"start": v(-16.21, 2.73) * mm, "end": v(-12.84, 6.1) * mm});
            skLineSegment(sketch, "E336", {"start": v(-12.84, 6.1) * mm, "end": v(-10.2, 6.1) * mm});
            skLineSegment(sketch, "E337", {"start": v(-9.8, 6.1) * mm, "end": v(-7.16, 6.1) * mm});
            skLineSegment(sketch, "E338", {"start": v(-6.1, 7.16) * mm, "end": v(-6.1, 9.8) * mm});
            skLineSegment(sketch, "E339", {"start": v(-6.1, 10.2) * mm, "end": v(-6.1, 12.84) * mm});
            skLineSegment(sketch, "E340", {"start": v(-6.1, 12.84) * mm, "end": v(-2.7, 16.24) * mm});
            skLineSegment(sketch, "E341", {"start": v(-2.7, 16.24) * mm, "end": v(-2.7, 18.2) * mm});
            skLineSegment(sketch, "E342", {"start": v(-2.7, 18.2) * mm, "end": v(0, 18.2) * mm});
            skLineSegment(sketch, "E343", {"start": v(0, 18.2) * mm, "end": v(2.7, 18.2) * mm});
            skCircle(sketch, "E344", {"center": v(-10, 10) * mm, "radius": 2.3 * mm});
            skCircle(sketch, "E345", {"center": v(10, 10) * mm, "radius": 2.3 * mm});
            skLineSegment(sketch, "E346", {"start": v(-6.1, 7.16) * mm, "end": v(-0.74, 1.8) * mm});
            skLineSegment(sketch, "E347", {"start": v(-1.8, 0.74) * mm, "end": v(-7.16, 6.1) * mm});
            skLineSegment(sketch, "E348", {"start": v(-1.8, 0.74) * mm, "end": v(-1.8, -2.7) * mm});
            skLineSegment(sketch, "E349", {"start": v(2.7, 1.8) * mm, "end": v(2.7, 3.76) * mm});
            skLineSegment(sketch, "E350", {"start": v(2.7, 3.76) * mm, "end": v(6.1, 7.16) * mm});
            skLineSegment(sketch, "E351", {"start": v(2.7, 1.8) * mm, "end": v(-0.74, 1.8) * mm});
            skLineSegment(sketch, "E352", {"start": v(6.1, 7.16) * mm, "end": v(6.1, 9.8) * mm});
            skLineSegment(sketch, "E353", {"start": v(6.1, 9.8) * mm, "end": v(6.3, 10) * mm});
            skLineSegment(sketch, "E354", {"start": v(6.3, 10) * mm, "end": v(6.1, 10.2) * mm});
            skLineSegment(sketch, "E355", {"start": v(6.1, 10.2) * mm, "end": v(6.1, 12.84) * mm});
            skLineSegment(sketch, "E356", {"start": v(-6.1, 10.2) * mm, "end": v(-6.3, 10) * mm});
            skLineSegment(sketch, "E357", {"start": v(-6.3, 10) * mm, "end": v(-6.1, 9.8) * mm});
            skLineSegment(sketch, "E358", {"start": v(-9.8, 6.1) * mm, "end": v(-10, 6.3) * mm});
            skLineSegment(sketch, "E359", {"start": v(-10, 6.3) * mm, "end": v(-10.2, 6.1) * mm});
            skLineSegment(sketch, "E360", {"start": v(-12.84, -6.1) * mm, "end": v(-10.2, -6.1) * mm});
            skLineSegment(sketch, "E361", {"start": v(-9.8, -6.1) * mm, "end": v(-7.16, -6.1) * mm});
            skCircle(sketch, "E362", {"center": v(-10, -10) * mm, "radius": 2.3 * mm});
            skLineSegment(sketch, "E363", {"start": v(-9.8, -6.1) * mm, "end": v(-10, -6.3) * mm});
            skLineSegment(sketch, "E364", {"start": v(-10, -6.3) * mm, "end": v(-10.2, -6.1) * mm});
            skLineSegment(sketch, "E365", {"start": v(-7.16, -6.1) * mm, "end": v(-3.79, -2.73) * mm});
            skLineSegment(sketch, "E366", {"start": v(-3.79, -2.73) * mm, "end": v(-1.8, -2.7) * mm});
            skLineSegment(sketch, "E367", {"start": v(16.56, 44.5) * mm, "end": v(18.2, 44.5) * mm});
            skLineSegment(sketch, "E368", {"start": v(18.2, 44.5) * mm, "end": v(18.2, 46.61) * mm});
            skLineSegment(sketch, "E369", {"start": v(18.2, 46.61) * mm, "end": v(18.8, 46.61) * mm});
            skLineSegment(sketch, "E370", {"start": v(18.8, 46.61) * mm, "end": v(19.82, 45.6) * mm});
            skArc(sketch, "E371", {"start": v(19.82, 45.6) * mm, "mid": v(19.95, 45.4) * mm, "end": v(20, 45.17) * mm});
            skLineSegment(sketch, "E372", {"start": v(20, 45.17) * mm, "end": v(20, 40.2) * mm});
            skLineSegment(sketch, "E373", {"start": v(20, 40.2) * mm, "end": v(19.8, 40) * mm});
            skLineSegment(sketch, "E374", {"start": v(19.8, 40) * mm, "end": v(20, 39.8) * mm});
            skLineSegment(sketch, "E375", {"start": v(20, 39.8) * mm, "end": v(20, 34.83) * mm});
            skArc(sketch, "E376", {"start": v(20, 34.83) * mm, "mid": v(19.95, 34.6) * mm, "end": v(19.82, 34.4) * mm});
            skLineSegment(sketch, "E377", {"start": v(19.82, 34.4) * mm, "end": v(18.8, 33.39) * mm});
            skLineSegment(sketch, "E378", {"start": v(18.8, 33.39) * mm, "end": v(18.2, 33.39) * mm});
            skLineSegment(sketch, "E379", {"start": v(18.2, 33.39) * mm, "end": v(18.2, 35.5) * mm});
            skLineSegment(sketch, "E380", {"start": v(18.2, 35.5) * mm, "end": v(16.56, 35.5) * mm});
            skLineSegment(sketch, "E381", {"start": v(16.56, 35.5) * mm, "end": v(13.9, 32.84) * mm});
            skLineSegment(sketch, "E382", {"start": v(13.9, 32.84) * mm, "end": v(13.9, 30.2) * mm});
            skLineSegment(sketch, "E383", {"start": v(13.9, 30.2) * mm, "end": v(13.7, 30) * mm});
            skLineSegment(sketch, "E384", {"start": v(13.7, 30) * mm, "end": v(13.9, 29.8) * mm});
            skLineSegment(sketch, "E385", {"start": v(13.9, 29.8) * mm, "end": v(13.9, 27.16) * mm});
            skLineSegment(sketch, "E386", {"start": v(13.9, 27.16) * mm, "end": v(16.56, 24.5) * mm});
            skLineSegment(sketch, "E387", {"start": v(16.56, 24.5) * mm, "end": v(18.2, 24.5) * mm});
            skLineSegment(sketch, "E388", {"start": v(18.2, 24.5) * mm, "end": v(18.2, 26.61) * mm});
            skLineSegment(sketch, "E389", {"start": v(18.2, 26.61) * mm, "end": v(18.8, 26.61) * mm});
            skLineSegment(sketch, "E390", {"start": v(18.8, 26.61) * mm, "end": v(19.82, 25.6) * mm});
            skArc(sketch, "E391", {"start": v(19.82, 25.6) * mm, "mid": v(19.95, 25.4) * mm, "end": v(20, 25.17) * mm});
            skLineSegment(sketch, "E392", {"start": v(20, 25.17) * mm, "end": v(20, 21.5) * mm});
            skArc(sketch, "E393", {"start": v(20, 21.5) * mm, "mid": v(19.56, 20.44) * mm, "end": v(18.5, 20) * mm});
            skArc(sketch, "E394", {"start": v(14.83, 20) * mm, "mid": v(14.6, 20.05) * mm, "end": v(14.4, 20.18) * mm});
            skLineSegment(sketch, "E395", {"start": v(14.4, 20.18) * mm, "end": v(13.39, 21.2) * mm});
            skLineSegment(sketch, "E396", {"start": v(13.39, 21.2) * mm, "end": v(13.39, 21.8) * mm});
            skLineSegment(sketch, "E397", {"start": v(13.39, 21.8) * mm, "end": v(15.5, 21.8) * mm});
            skLineSegment(sketch, "E398", {"start": v(15.5, 21.8) * mm, "end": v(15.5, 23.44) * mm});
            skLineSegment(sketch, "E399", {"start": v(15.5, 23.44) * mm, "end": v(12.84, 26.1) * mm});
            skLineSegment(sketch, "E400", {"start": v(12.84, 26.1) * mm, "end": v(10.2, 26.1) * mm});
            skLineSegment(sketch, "E401", {"start": v(10.2, 26.1) * mm, "end": v(10, 26.3) * mm});
            skLineSegment(sketch, "E402", {"start": v(10, 26.3) * mm, "end": v(9.8, 26.1) * mm});
            skLineSegment(sketch, "E403", {"start": v(9.8, 26.1) * mm, "end": v(7.16, 26.1) * mm});
            skLineSegment(sketch, "E404", {"start": v(7.16, 26.1) * mm, "end": v(4.5, 23.44) * mm});
            skLineSegment(sketch, "E405", {"start": v(4.5, 23.44) * mm, "end": v(4.5, 21.8) * mm});
            skLineSegment(sketch, "E406", {"start": v(4.5, 21.8) * mm, "end": v(6.61, 21.8) * mm});
            skLineSegment(sketch, "E407", {"start": v(6.61, 21.8) * mm, "end": v(6.61, 21.2) * mm});
            skLineSegment(sketch, "E408", {"start": v(6.61, 21.2) * mm, "end": v(5.6, 20.18) * mm});
            skArc(sketch, "E409", {"start": v(5.6, 20.18) * mm, "mid": v(5.4, 20.05) * mm, "end": v(5.17, 20) * mm});
            skLineSegment(sketch, "E410", {"start": v(0.2, 20) * mm, "end": v(0, 20.2) * mm});
            skLineSegment(sketch, "E411", {"start": v(0, 20.2) * mm, "end": v(-0.2, 20) * mm});
            skArc(sketch, "E412", {"start": v(-5.17, 20) * mm, "mid": v(-5.4, 20.05) * mm, "end": v(-5.6, 20.18) * mm});
            skLineSegment(sketch, "E413", {"start": v(-5.6, 20.18) * mm, "end": v(-6.61, 21.2) * mm});
            skLineSegment(sketch, "E414", {"start": v(-6.61, 21.2) * mm, "end": v(-6.61, 21.8) * mm});
            skLineSegment(sketch, "E415", {"start": v(-6.61, 21.8) * mm, "end": v(-4.5, 21.8) * mm});
            skLineSegment(sketch, "E416", {"start": v(-4.5, 21.8) * mm, "end": v(-4.5, 23.44) * mm});
            skLineSegment(sketch, "E417", {"start": v(-4.5, 23.44) * mm, "end": v(-7.16, 26.1) * mm});
            skLineSegment(sketch, "E418", {"start": v(-7.16, 26.1) * mm, "end": v(-9.8, 26.1) * mm});
            skLineSegment(sketch, "E419", {"start": v(-9.8, 26.1) * mm, "end": v(-10, 26.3) * mm});
            skLineSegment(sketch, "E420", {"start": v(-10, 26.3) * mm, "end": v(-10.2, 26.1) * mm});
            skLineSegment(sketch, "E421", {"start": v(-10.2, 26.1) * mm, "end": v(-12.84, 26.1) * mm});
            skLineSegment(sketch, "E422", {"start": v(-12.84, 26.1) * mm, "end": v(-15.5, 23.44) * mm});
            skLineSegment(sketch, "E423", {"start": v(-15.5, 23.44) * mm, "end": v(-15.5, 21.8) * mm});
            skLineSegment(sketch, "E424", {"start": v(-15.5, 21.8) * mm, "end": v(-13.39, 21.8) * mm});
            skLineSegment(sketch, "E425", {"start": v(-13.39, 21.8) * mm, "end": v(-13.39, 21.2) * mm});
            skLineSegment(sketch, "E426", {"start": v(-13.39, 21.2) * mm, "end": v(-14.4, 20.18) * mm});
            skArc(sketch, "E427", {"start": v(-14.4, 20.18) * mm, "mid": v(-14.6, 20.05) * mm, "end": v(-14.83, 20) * mm});
            skArc(sketch, "E428", {"start": v(-18.5, 20) * mm, "mid": v(-19.56, 20.44) * mm, "end": v(-20, 21.5) * mm});
            skLineSegment(sketch, "E429", {"start": v(-20, 21.5) * mm, "end": v(-20, 25.17) * mm});
            skArc(sketch, "E430", {"start": v(-20, 25.17) * mm, "mid": v(-19.95, 25.4) * mm, "end": v(-19.82, 25.6) * mm});
            skLineSegment(sketch, "E431", {"start": v(-19.82, 25.6) * mm, "end": v(-18.8, 26.61) * mm});
            skLineSegment(sketch, "E432", {"start": v(-18.8, 26.61) * mm, "end": v(-18.2, 26.61) * mm});
            skLineSegment(sketch, "E433", {"start": v(-18.2, 26.61) * mm, "end": v(-18.2, 24.5) * mm});
            skLineSegment(sketch, "E434", {"start": v(-18.2, 24.5) * mm, "end": v(-16.56, 24.5) * mm});
            skLineSegment(sketch, "E435", {"start": v(-16.56, 24.5) * mm, "end": v(-13.9, 27.16) * mm});
            skLineSegment(sketch, "E436", {"start": v(-13.9, 27.16) * mm, "end": v(-13.9, 29.8) * mm});
            skLineSegment(sketch, "E437", {"start": v(-13.9, 29.8) * mm, "end": v(-13.7, 30) * mm});
            skLineSegment(sketch, "E438", {"start": v(-13.7, 30) * mm, "end": v(-13.9, 30.2) * mm});
            skLineSegment(sketch, "E439", {"start": v(-13.9, 30.2) * mm, "end": v(-13.9, 32.84) * mm});
            skLineSegment(sketch, "E440", {"start": v(-13.9, 32.84) * mm, "end": v(-16.56, 35.5) * mm});
            skLineSegment(sketch, "E441", {"start": v(-16.56, 35.5) * mm, "end": v(-18.2, 35.5) * mm});
            skLineSegment(sketch, "E442", {"start": v(-18.2, 35.5) * mm, "end": v(-18.2, 33.39) * mm});
            skLineSegment(sketch, "E443", {"start": v(-18.2, 33.39) * mm, "end": v(-18.8, 33.39) * mm});
            skLineSegment(sketch, "E444", {"start": v(-18.8, 33.39) * mm, "end": v(-19.82, 34.4) * mm});
            skArc(sketch, "E445", {"start": v(-19.82, 34.4) * mm, "mid": v(-19.95, 34.6) * mm, "end": v(-20, 34.83) * mm});
            skLineSegment(sketch, "E446", {"start": v(-20, 34.83) * mm, "end": v(-20, 39.8) * mm});
            skLineSegment(sketch, "E447", {"start": v(-20, 39.8) * mm, "end": v(-19.8, 40) * mm});
            skLineSegment(sketch, "E448", {"start": v(-19.8, 40) * mm, "end": v(-20, 40.2) * mm});
            skLineSegment(sketch, "E449", {"start": v(-20, 40.2) * mm, "end": v(-20, 45.17) * mm});
            skArc(sketch, "E450", {"start": v(-20, 45.17) * mm, "mid": v(-19.95, 45.4) * mm, "end": v(-19.82, 45.6) * mm});
            skLineSegment(sketch, "E451", {"start": v(-19.82, 45.6) * mm, "end": v(-18.8, 46.61) * mm});
            skLineSegment(sketch, "E452", {"start": v(-18.8, 46.61) * mm, "end": v(-18.2, 46.61) * mm});
            skLineSegment(sketch, "E453", {"start": v(-18.2, 46.61) * mm, "end": v(-18.2, 44.5) * mm});
            skLineSegment(sketch, "E454", {"start": v(-18.2, 44.5) * mm, "end": v(-16.56, 44.5) * mm});
            skLineSegment(sketch, "E455", {"start": v(-16.56, 44.5) * mm, "end": v(-13.9, 47.16) * mm});
            skLineSegment(sketch, "E456", {"start": v(-13.9, 47.16) * mm, "end": v(-13.9, 49.8) * mm});
            skLineSegment(sketch, "E457", {"start": v(-13.9, 49.8) * mm, "end": v(-13.7, 50) * mm});
            skLineSegment(sketch, "E458", {"start": v(-13.7, 50) * mm, "end": v(-13.9, 50.2) * mm});
            skLineSegment(sketch, "E459", {"start": v(-13.9, 50.2) * mm, "end": v(-13.9, 52.84) * mm});
            skLineSegment(sketch, "E460", {"start": v(-13.9, 52.84) * mm, "end": v(-16.56, 55.5) * mm});
            skLineSegment(sketch, "E461", {"start": v(-16.56, 55.5) * mm, "end": v(-18.2, 55.5) * mm});
            skLineSegment(sketch, "E462", {"start": v(-18.2, 55.5) * mm, "end": v(-18.2, 53.39) * mm});
            skLineSegment(sketch, "E463", {"start": v(-18.2, 53.39) * mm, "end": v(-18.8, 53.39) * mm});
            skLineSegment(sketch, "E464", {"start": v(-18.8, 53.39) * mm, "end": v(-19.82, 54.4) * mm});
            skArc(sketch, "E465", {"start": v(-19.82, 54.4) * mm, "mid": v(-19.95, 54.6) * mm, "end": v(-20, 54.83) * mm});
            skLineSegment(sketch, "E466", {"start": v(-20, 54.83) * mm, "end": v(-20, 58.5) * mm});
            skArc(sketch, "E467", {"start": v(-20, 58.5) * mm, "mid": v(-19.56, 59.56) * mm, "end": v(-18.5, 60) * mm});
            skLineSegment(sketch, "E468", {"start": v(-18.5, 60) * mm, "end": v(-14.83, 60) * mm});
            skArc(sketch, "E469", {"start": v(-14.83, 60) * mm, "mid": v(-14.6, 59.95) * mm, "end": v(-14.4, 59.82) * mm});
            skLineSegment(sketch, "E470", {"start": v(-14.4, 59.82) * mm, "end": v(-13.39, 58.8) * mm});
            skLineSegment(sketch, "E471", {"start": v(-13.39, 58.8) * mm, "end": v(-13.39, 58.2) * mm});
            skLineSegment(sketch, "E472", {"start": v(-13.39, 58.2) * mm, "end": v(-15.5, 58.2) * mm});
            skLineSegment(sketch, "E473", {"start": v(-15.5, 58.2) * mm, "end": v(-15.5, 56.56) * mm});
            skLineSegment(sketch, "E474", {"start": v(-15.5, 56.56) * mm, "end": v(-12.84, 53.9) * mm});
            skLineSegment(sketch, "E475", {"start": v(-12.84, 53.9) * mm, "end": v(-10.2, 53.9) * mm});
            skLineSegment(sketch, "E476", {"start": v(-10.2, 53.9) * mm, "end": v(-10, 53.7) * mm});
            skLineSegment(sketch, "E477", {"start": v(-10, 53.7) * mm, "end": v(-9.8, 53.9) * mm});
            skLineSegment(sketch, "E478", {"start": v(-9.8, 53.9) * mm, "end": v(-7.16, 53.9) * mm});
            skLineSegment(sketch, "E479", {"start": v(-7.16, 53.9) * mm, "end": v(-4.5, 56.56) * mm});
            skLineSegment(sketch, "E480", {"start": v(-4.5, 56.56) * mm, "end": v(-4.5, 58.2) * mm});
            skLineSegment(sketch, "E481", {"start": v(-4.5, 58.2) * mm, "end": v(-6.61, 58.2) * mm});
            skLineSegment(sketch, "E482", {"start": v(-6.61, 58.2) * mm, "end": v(-6.61, 58.8) * mm});
            skLineSegment(sketch, "E483", {"start": v(-6.61, 58.8) * mm, "end": v(-5.6, 59.82) * mm});
            skArc(sketch, "E484", {"start": v(-5.6, 59.82) * mm, "mid": v(-5.4, 59.95) * mm, "end": v(-5.17, 60) * mm});
            skLineSegment(sketch, "E485", {"start": v(-5.17, 60) * mm, "end": v(-0.2, 60) * mm});
            skLineSegment(sketch, "E486", {"start": v(-0.2, 60) * mm, "end": v(0, 59.8) * mm});
            skLineSegment(sketch, "E487", {"start": v(0, 59.8) * mm, "end": v(0.2, 60) * mm});
            skLineSegment(sketch, "E488", {"start": v(0.2, 60) * mm, "end": v(5.17, 60) * mm});
            skArc(sketch, "E489", {"start": v(5.17, 60) * mm, "mid": v(5.4, 59.95) * mm, "end": v(5.6, 59.82) * mm});
            skLineSegment(sketch, "E490", {"start": v(5.6, 59.82) * mm, "end": v(6.61, 58.8) * mm});
            skLineSegment(sketch, "E491", {"start": v(6.61, 58.8) * mm, "end": v(6.61, 58.2) * mm});
            skLineSegment(sketch, "E492", {"start": v(6.61, 58.2) * mm, "end": v(4.5, 58.2) * mm});
            skLineSegment(sketch, "E493", {"start": v(4.5, 58.2) * mm, "end": v(4.5, 56.56) * mm});
            skLineSegment(sketch, "E494", {"start": v(4.5, 56.56) * mm, "end": v(7.16, 53.9) * mm});
            skLineSegment(sketch, "E495", {"start": v(7.16, 53.9) * mm, "end": v(9.8, 53.9) * mm});
            skLineSegment(sketch, "E496", {"start": v(9.8, 53.9) * mm, "end": v(10, 53.7) * mm});
            skLineSegment(sketch, "E497", {"start": v(10, 53.7) * mm, "end": v(10.2, 53.9) * mm});
            skLineSegment(sketch, "E498", {"start": v(10.2, 53.9) * mm, "end": v(12.84, 53.9) * mm});
            skLineSegment(sketch, "E499", {"start": v(12.84, 53.9) * mm, "end": v(15.5, 56.56) * mm});
            skLineSegment(sketch, "E500", {"start": v(15.5, 56.56) * mm, "end": v(15.5, 58.2) * mm});
            skLineSegment(sketch, "E501", {"start": v(15.5, 58.2) * mm, "end": v(13.39, 58.2) * mm});
            skLineSegment(sketch, "E502", {"start": v(13.39, 58.2) * mm, "end": v(13.39, 58.8) * mm});
            skLineSegment(sketch, "E503", {"start": v(13.39, 58.8) * mm, "end": v(14.4, 59.82) * mm});
            skArc(sketch, "E504", {"start": v(14.4, 59.82) * mm, "mid": v(14.6, 59.95) * mm, "end": v(14.83, 60) * mm});
            skLineSegment(sketch, "E505", {"start": v(14.83, 60) * mm, "end": v(18.5, 60) * mm});
            skArc(sketch, "E506", {"start": v(18.5, 60) * mm, "mid": v(19.56, 59.56) * mm, "end": v(20, 58.5) * mm});
            skLineSegment(sketch, "E507", {"start": v(20, 58.5) * mm, "end": v(20, 54.83) * mm});
            skArc(sketch, "E508", {"start": v(20, 54.83) * mm, "mid": v(19.95, 54.6) * mm, "end": v(19.82, 54.4) * mm});
            skLineSegment(sketch, "E509", {"start": v(19.82, 54.4) * mm, "end": v(18.8, 53.39) * mm});
            skLineSegment(sketch, "E510", {"start": v(18.8, 53.39) * mm, "end": v(18.2, 53.39) * mm});
            skLineSegment(sketch, "E511", {"start": v(18.2, 53.39) * mm, "end": v(18.2, 55.5) * mm});
            skLineSegment(sketch, "E512", {"start": v(18.2, 55.5) * mm, "end": v(16.56, 55.5) * mm});
            skLineSegment(sketch, "E513", {"start": v(16.56, 55.5) * mm, "end": v(13.9, 52.84) * mm});
            skLineSegment(sketch, "E514", {"start": v(13.9, 52.84) * mm, "end": v(13.9, 50.2) * mm});
            skLineSegment(sketch, "E515", {"start": v(13.9, 50.2) * mm, "end": v(13.7, 50) * mm});
            skLineSegment(sketch, "E516", {"start": v(13.7, 50) * mm, "end": v(13.9, 49.8) * mm});
            skLineSegment(sketch, "E517", {"start": v(13.9, 49.8) * mm, "end": v(13.9, 47.16) * mm});
            skLineSegment(sketch, "E518", {"start": v(13.9, 47.16) * mm, "end": v(16.56, 44.5) * mm});
            skCircle(sketch, "E519", {"center": v(-10, 30) * mm, "radius": 2.3 * mm});
            skCircle(sketch, "E520", {"center": v(-10, 50) * mm, "radius": 2.3 * mm});
            skLineSegment(sketch, "E521", {"start": v(18.2, 42.7) * mm, "end": v(16.24, 42.7) * mm});
            skLineSegment(sketch, "E522", {"start": v(16.24, 42.7) * mm, "end": v(12.84, 46.1) * mm});
            skLineSegment(sketch, "E523", {"start": v(12.84, 46.1) * mm, "end": v(10, 46.1) * mm});
            skArc(sketch, "E524", {"start": v(10, 46.1) * mm, "mid": v(7.24, 47.24) * mm, "end": v(6.1, 50) * mm});
            skLineSegment(sketch, "E525", {"start": v(6.1, 50) * mm, "end": v(6.1, 52.84) * mm});
            skLineSegment(sketch, "E526", {"start": v(6.1, 52.84) * mm, "end": v(2.73, 56.21) * mm});
            skLineSegment(sketch, "E527", {"start": v(2.73, 56.21) * mm, "end": v(2.7, 58.2) * mm});
            skLineSegment(sketch, "E528", {"start": v(2.7, 58.2) * mm, "end": v(0, 58.2) * mm});
            skLineSegment(sketch, "E529", {"start": v(0, 58.2) * mm, "end": v(-2.7, 58.2) * mm});
            skLineSegment(sketch, "E530", {"start": v(-2.7, 58.2) * mm, "end": v(-2.73, 56.21) * mm});
            skLineSegment(sketch, "E531", {"start": v(-2.73, 56.21) * mm, "end": v(-6.1, 52.84) * mm});
            skLineSegment(sketch, "E532", {"start": v(-6.1, 52.84) * mm, "end": v(-6.1, 50) * mm});
            skArc(sketch, "E533", {"start": v(-6.1, 50) * mm, "mid": v(-7.24, 47.24) * mm, "end": v(-10, 46.1) * mm});
            skLineSegment(sketch, "E534", {"start": v(-10, 46.1) * mm, "end": v(-12.84, 46.1) * mm});
            skLineSegment(sketch, "E535", {"start": v(-12.84, 46.1) * mm, "end": v(-16.24, 42.7) * mm});
            skLineSegment(sketch, "E536", {"start": v(-16.24, 42.7) * mm, "end": v(-18.2, 42.7) * mm});
            skLineSegment(sketch, "E537", {"start": v(-18.2, 42.7) * mm, "end": v(-18.2, 40) * mm});
            skLineSegment(sketch, "E538", {"start": v(-18.2, 40) * mm, "end": v(-18.2, 37.3) * mm});
            skLineSegment(sketch, "E539", {"start": v(-18.2, 37.3) * mm, "end": v(-16.24, 37.3) * mm});
            skLineSegment(sketch, "E540", {"start": v(-16.24, 37.3) * mm, "end": v(-12.84, 33.9) * mm});
            skLineSegment(sketch, "E541", {"start": v(-12.84, 33.9) * mm, "end": v(-10, 33.9) * mm});
            skArc(sketch, "E542", {"start": v(-10, 33.9) * mm, "mid": v(-7.24, 32.76) * mm, "end": v(-6.1, 30) * mm});
            skLineSegment(sketch, "E543", {"start": v(-6.1, 30) * mm, "end": v(-6.1, 27.16) * mm});
            skLineSegment(sketch, "E544", {"start": v(-6.1, 27.16) * mm, "end": v(-2.73, 23.79) * mm});
            skLineSegment(sketch, "E545", {"start": v(-2.73, 23.79) * mm, "end": v(-2.7, 21.8) * mm});
            skLineSegment(sketch, "E546", {"start": v(-2.7, 21.8) * mm, "end": v(0, 21.8) * mm});
            skLineSegment(sketch, "E547", {"start": v(0, 21.8) * mm, "end": v(2.7, 21.8) * mm});
            skLineSegment(sketch, "E548", {"start": v(2.7, 21.8) * mm, "end": v(2.73, 23.79) * mm});
            skLineSegment(sketch, "E549", {"start": v(2.73, 23.79) * mm, "end": v(6.1, 27.16) * mm});
            skLineSegment(sketch, "E550", {"start": v(6.1, 27.16) * mm, "end": v(6.1, 30) * mm});
            skArc(sketch, "E551", {"start": v(6.1, 30) * mm, "mid": v(7.24, 32.76) * mm, "end": v(10, 33.9) * mm});
            skLineSegment(sketch, "E552", {"start": v(10, 33.9) * mm, "end": v(12.84, 33.9) * mm});
            skLineSegment(sketch, "E553", {"start": v(12.84, 33.9) * mm, "end": v(16.24, 37.3) * mm});
            skLineSegment(sketch, "E554", {"start": v(16.24, 37.3) * mm, "end": v(18.2, 37.3) * mm});
            skLineSegment(sketch, "E555", {"start": v(18.2, 37.3) * mm, "end": v(18.2, 40) * mm});
            skLineSegment(sketch, "E556", {"start": v(18.2, 40) * mm, "end": v(18.2, 42.7) * mm});
            skCircle(sketch, "E557", {"center": v(10, 30) * mm, "radius": 2.3 * mm});
            skCircle(sketch, "E558", {"center": v(10, 50) * mm, "radius": 2.3 * mm});
            skSolve(sketch);
        }
        {
            var Q0;
            Q0 = qSketchRegion(id + "F0", true);
            extrude(context, id + "F1", {"entities" : qUnion([Q0]), "endBound" : BoundingType.SYMMETRIC, "depth" : 2000 * mm});
        }
        {
            var Q0;
            Q0=qCreatedBy(makeId("Front.planeOp"),FACE);
            var sketch = newSketch(context, id + "F2", { "sketchPlane" : qUnion([Q0])});
            skLineSegment(sketch, "E559", {"start": v(-20, 58.5) * mm, "end": v(-20, 54.83) * mm, "construction": true});
            skLineSegment(sketch, "E560", {"start": v(-14.83, 60) * mm, "end": v(-18.5, 60) * mm, "construction": true});
            skLineSegment(sketch, "E561", {"start": v(-20, 41.01) * mm, "end": v(-20, 60) * mm});
            skLineSegment(sketch, "E562", {"start": v(-20, 60) * mm, "end": v(-18.13, 60) * mm});
            skLineSegment(sketch, "E563", {"start": v(-17.63, 60.5) * mm, "end": v(-17.63, 60.55) * mm});
            skLineSegment(sketch, "E564", {"start": v(-17.78, 60.9) * mm, "end": v(-19.65, 62.77) * mm});
            skLineSegment(sketch, "E565", {"start": v(-20.35, 62.77) * mm, "end": v(-22.22, 60.9) * mm});
            skLineSegment(sketch, "E566", {"start": v(-22.37, 60.55) * mm, "end": v(-22.37, 41.01) * mm});
            skLineSegment(sketch, "E567", {"start": v(-21.87, 40.51) * mm, "end": v(-20.5, 40.51) * mm});
            skPoint(sketch, "E568.visualSharp", {"position": v(-17.63, 60) * mm});
            skArc(sketch, "E568.filletArc", {"start": v(-18.13, 60) * mm, "mid": v(-17.78, 60.15) * mm, "end": v(-17.63, 60.5) * mm});
            skPoint(sketch, "E569.visualSharp", {"position": v(-17.63, 60.76) * mm});
            skArc(sketch, "E569.filletArc", {"start": v(-17.63, 60.55) * mm, "mid": v(-17.67, 60.74) * mm, "end": v(-17.78, 60.9) * mm});
            skPoint(sketch, "E570.visualSharp", {"position": v(-20, 63.13) * mm});
            skArc(sketch, "E570.filletArc", {"start": v(-19.65, 62.77) * mm, "mid": v(-20, 62.92) * mm, "end": v(-20.35, 62.77) * mm});
            skPoint(sketch, "E571.visualSharp", {"position": v(-22.37, 60.76) * mm});
            skArc(sketch, "E571.filletArc", {"start": v(-22.22, 60.9) * mm, "mid": v(-22.33, 60.74) * mm, "end": v(-22.37, 60.55) * mm});
            skPoint(sketch, "E572.visualSharp", {"position": v(-22.37, 40.51) * mm});
            skArc(sketch, "E572.filletArc", {"start": v(-22.37, 41.01) * mm, "mid": v(-22.22, 40.66) * mm, "end": v(-21.87, 40.51) * mm});
            skPoint(sketch, "E573.visualSharp", {"position": v(-20, 40.51) * mm});
            skArc(sketch, "E573.filletArc", {"start": v(-20.5, 40.51) * mm, "mid": v(-20.15, 40.66) * mm, "end": v(-20, 41.01) * mm});
            skLineSegment(sketch, "E574", {"start": v(-20, 63.13) * mm, "end": v(-20, 62.42) * mm, "construction": true});
            skLineSegment(sketch, "E575", {"start": v(-14.83, -60) * mm, "end": v(-18.5, -60) * mm, "construction": true});
            skLineSegment(sketch, "E576", {"start": v(-20, -58.5) * mm, "end": v(-20, -54.83) * mm, "construction": true});
            skLineSegment(sketch, "E577", {"start": v(-48.11, 0) * mm, "end": v(15.41, 0) * mm, "construction": true});
            skArc(sketch, "E578.MirrorCS", {"start": v(-17.63, -60.55) * mm, "mid": v(-17.67, -60.74) * mm, "end": v(-17.78, -60.9) * mm});
            skLineSegment(sketch, "E579.MirrorCS", {"start": v(-17.63, -60.5) * mm, "end": v(-17.63, -60.55) * mm});
            skArc(sketch, "E580.MirrorCS", {"start": v(-18.13, -60) * mm, "mid": v(-17.78, -60.15) * mm, "end": v(-17.63, -60.5) * mm});
            skArc(sketch, "E581.MirrorCS", {"start": v(-22.37, -41) * mm, "mid": v(-22.22, -40.66) * mm, "end": v(-21.87, -40.5) * mm});
            skArc(sketch, "E582.MirrorCS", {"start": v(-20.5, -40.5) * mm, "mid": v(-20.15, -40.66) * mm, "end": v(-20, -41) * mm});
            skLineSegment(sketch, "E583.MirrorCS", {"start": v(-20, -63.13) * mm, "end": v(-20, -62.42) * mm, "construction": true});
            skArc(sketch, "E584.MirrorCS", {"start": v(-22.22, -60.9) * mm, "mid": v(-22.33, -60.74) * mm, "end": v(-22.37, -60.55) * mm});
            skArc(sketch, "E585.MirrorCS", {"start": v(-19.65, -62.77) * mm, "mid": v(-20, -62.92) * mm, "end": v(-20.35, -62.77) * mm});
            skLineSegment(sketch, "E586.MirrorCS", {"start": v(-21.87, -40.5) * mm, "end": v(-20.5, -40.5) * mm});
            skLineSegment(sketch, "E587.MirrorCS", {"start": v(-20, -60) * mm, "end": v(-18.13, -60) * mm});
            skLineSegment(sketch, "E588.MirrorCS", {"start": v(-17.78, -60.9) * mm, "end": v(-19.65, -62.77) * mm});
            skPoint(sketch, "E589.MirrorP", {"position": v(-17.63, -60.76) * mm});
            skPoint(sketch, "E590.MirrorP", {"position": v(-22.37, -60.76) * mm});
            skPoint(sketch, "E591.MirrorP", {"position": v(-22.37, -40.5) * mm});
            skPoint(sketch, "E592.MirrorP", {"position": v(-17.63, -60) * mm});
            skPoint(sketch, "E593.MirrorP", {"position": v(-20, -63.13) * mm});
            skPoint(sketch, "E594.MirrorP", {"position": v(-20, -40.5) * mm});
            skLineSegment(sketch, "E595.MirrorCS", {"start": v(-20, -41) * mm, "end": v(-20, -60) * mm});
            skLineSegment(sketch, "E596.MirrorCS", {"start": v(-20.35, -62.77) * mm, "end": v(-22.22, -60.9) * mm});
            skLineSegment(sketch, "E597.MirrorCS", {"start": v(-22.37, -60.55) * mm, "end": v(-22.37, -41) * mm});
            skSolve(sketch);
        }
        {
            var Q0;
            Q0 = qSketchRegion(id + "F2", true);
            extrude(context, id + "F3", {"entities" : qUnion([Q0]), "endBound" : BoundingType.SYMMETRIC, "depth" : 2000 * mm});
        }
        {
            var Q0;
            Q0=qCreatedBy(makeId("Front.planeOp"),FACE);
            var sketch = newSketch(context, id + "F4", { "sketchPlane" : qUnion([Q0])});
            skLineSegment(sketch, "E598", {"start": v(-20.5, 79.57) * mm, "end": v(-20.5, 80.62) * mm});
            skLineSegment(sketch, "E599", {"start": v(-20.5, 80.62) * mm, "end": v(-24.82, 80.62) * mm});
            skLineSegment(sketch, "E600", {"start": v(-24.82, 80.62) * mm, "end": v(-25.12, 80.63) * mm});
            skLineSegment(sketch, "E601", {"start": v(-25.12, 80.63) * mm, "end": v(-25.12, 82.4) * mm});
            skLineSegment(sketch, "E602", {"start": v(-25.12, 82.4) * mm, "end": v(-22.95, 84.57) * mm});
            skLineSegment(sketch, "E603", {"start": v(-22.45, 84.57) * mm, "end": v(-20.28, 82.39) * mm});
            skLineSegment(sketch, "E604", {"start": v(-20.5, 79.57) * mm, "end": v(-19.5, 79.57) * mm});
            skLineSegment(sketch, "E605", {"start": v(-20.28, 82.39) * mm, "end": v(-20.28, 82) * mm});
            skLineSegment(sketch, "E606", {"start": v(-20.28, 82) * mm, "end": v(-20, 82) * mm});
            skLineSegment(sketch, "E607", {"start": v(-20, 82) * mm, "end": v(-19.73, 82) * mm});
            skLineSegment(sketch, "E608", {"start": v(-19.73, 82) * mm, "end": v(-19.73, 82.39) * mm});
            skLineSegment(sketch, "E609", {"start": v(-19.73, 82.39) * mm, "end": v(-17.55, 84.57) * mm});
            skLineSegment(sketch, "E610", {"start": v(-17.05, 84.57) * mm, "end": v(-14.88, 82.4) * mm});
            skLineSegment(sketch, "E611", {"start": v(-14.88, 82.4) * mm, "end": v(-14.88, 80.63) * mm});
            skLineSegment(sketch, "E612", {"start": v(-14.88, 80.63) * mm, "end": v(-15.18, 80.62) * mm});
            skLineSegment(sketch, "E613", {"start": v(-15.18, 80.62) * mm, "end": v(-19.5, 80.62) * mm});
            skLineSegment(sketch, "E614", {"start": v(-19.5, 80.62) * mm, "end": v(-19.5, 79.57) * mm});
            skLineSegment(sketch, "E615", {"start": v(-22.95, 84.57) * mm, "end": v(-22.45, 84.57) * mm});
            skPoint(sketch, "E616.orphan", {"position": v(-22.7, 84.82) * mm});
            skPoint(sketch, "E617.orphan", {"position": v(-17.3, 84.82) * mm});
            skLineSegment(sketch, "E618.trimOffspring", {"start": v(-17.55, 84.57) * mm, "end": v(-17.05, 84.57) * mm});
            skLineSegment(sketch, "E619", {"start": v(-20, 79.57) * mm, "end": v(-20, 82) * mm, "construction": true});
            skLineSegment(sketch, "E620", {"start": v(-36.2, 72.62) * mm, "end": v(-8.78, 72.62) * mm, "construction": true});
            skLineSegment(sketch, "E621.MirrorCS", {"start": v(-20.28, 63.25) * mm, "end": v(-20, 63.25) * mm});
            skLineSegment(sketch, "E622.MirrorCS", {"start": v(-20.28, 62.85) * mm, "end": v(-20.28, 63.25) * mm});
            skLineSegment(sketch, "E623.MirrorCS", {"start": v(-20, 63.25) * mm, "end": v(-19.73, 63.25) * mm});
            skLineSegment(sketch, "E624.MirrorCS", {"start": v(-19.73, 63.25) * mm, "end": v(-19.73, 62.85) * mm});
            skLineSegment(sketch, "E625.MirrorCS", {"start": v(-20.5, 65.68) * mm, "end": v(-19.5, 65.68) * mm});
            skLineSegment(sketch, "E626.MirrorCS", {"start": v(-22.95, 60.68) * mm, "end": v(-22.45, 60.68) * mm});
            skLineSegment(sketch, "E627.MirrorCS", {"start": v(-20, 65.68) * mm, "end": v(-20, 63.25) * mm, "construction": true});
            skLineSegment(sketch, "E628.MirrorCS", {"start": v(-20.5, 65.68) * mm, "end": v(-20.5, 64.62) * mm});
            skLineSegment(sketch, "E629.MirrorCS", {"start": v(-19.5, 64.62) * mm, "end": v(-19.5, 65.68) * mm});
            skLineSegment(sketch, "E630.MirrorCS", {"start": v(-17.55, 60.68) * mm, "end": v(-17.05, 60.68) * mm});
            skLineSegment(sketch, "E631.MirrorCS", {"start": v(-25.12, 64.61) * mm, "end": v(-25.12, 62.84) * mm});
            skLineSegment(sketch, "E632.MirrorCS", {"start": v(-24.82, 64.62) * mm, "end": v(-25.12, 64.61) * mm});
            skLineSegment(sketch, "E633.MirrorCS", {"start": v(-14.88, 62.84) * mm, "end": v(-14.88, 64.61) * mm});
            skLineSegment(sketch, "E634.MirrorCS", {"start": v(-14.88, 64.61) * mm, "end": v(-15.18, 64.62) * mm});
            skLineSegment(sketch, "E635.MirrorCS", {"start": v(-25.12, 62.84) * mm, "end": v(-22.95, 60.68) * mm});
            skLineSegment(sketch, "E636.MirrorCS", {"start": v(-20.5, 64.62) * mm, "end": v(-24.82, 64.62) * mm});
            skLineSegment(sketch, "E637.MirrorCS", {"start": v(-19.73, 62.85) * mm, "end": v(-17.55, 60.68) * mm});
            skLineSegment(sketch, "E638.MirrorCS", {"start": v(-22.45, 60.68) * mm, "end": v(-20.27, 62.85) * mm});
            skLineSegment(sketch, "E639.MirrorCS", {"start": v(-15.18, 64.62) * mm, "end": v(-19.5, 64.62) * mm});
            skPoint(sketch, "E640.MirrorP", {"position": v(-22.7, 60.43) * mm});
            skPoint(sketch, "E641.MirrorP", {"position": v(-17.3, 60.43) * mm});
            skLineSegment(sketch, "E642.MirrorCS", {"start": v(-17.05, 60.68) * mm, "end": v(-14.88, 62.84) * mm});
            skSolve(sketch);
        }
        {
            var Q0;
            Q0 = qSketchRegion(id + "F4", true);
            var Q1;
            Q1=sQuery(id+"F4.wireOp",EDGE,"E620");
            revolve(context, id + "F5", {"entities" : qUnion([Q0]), "axis" : qUnion([Q1]), "revolveType" : RevolveType.FULL});
        }
        {
            var Q0;
            Q0=qCreatedBy(makeId("Front.planeOp"),FACE);
            var sketch = newSketch(context, id + "F6", { "sketchPlane" : qUnion([Q0])});
            skLineSegment(sketch, "E643", {"start": v(-20.5, -65.68) * mm, "end": v(-20.5, -64.62) * mm});
            skLineSegment(sketch, "E644", {"start": v(-20.5, -64.62) * mm, "end": v(-24.9, -64.62) * mm});
            skLineSegment(sketch, "E645", {"start": v(-24.9, -64.62) * mm, "end": v(-25.12, -64.41) * mm});
            skLineSegment(sketch, "E646", {"start": v(-25.12, -64.41) * mm, "end": v(-25.12, -62.84) * mm});
            skLineSegment(sketch, "E647", {"start": v(-25.12, -62.84) * mm, "end": v(-22.95, -60.68) * mm});
            skLineSegment(sketch, "E648", {"start": v(-22.45, -60.68) * mm, "end": v(-20.28, -62.85) * mm});
            skLineSegment(sketch, "E649", {"start": v(-13.43, -72.62) * mm, "end": v(-28.74, -72.62) * mm, "construction": true});
            skLineSegment(sketch, "E650", {"start": v(-20.5, -65.68) * mm, "end": v(-19.5, -65.68) * mm});
            skLineSegment(sketch, "E651", {"start": v(-20.28, -62.85) * mm, "end": v(-20.28, -63.25) * mm});
            skLineSegment(sketch, "E652", {"start": v(-20.28, -63.25) * mm, "end": v(-20, -63.25) * mm});
            skLineSegment(sketch, "E653", {"start": v(-20, -63.25) * mm, "end": v(-19.73, -63.25) * mm});
            skLineSegment(sketch, "E654", {"start": v(-19.73, -63.25) * mm, "end": v(-19.73, -62.85) * mm});
            skLineSegment(sketch, "E655", {"start": v(-19.73, -62.85) * mm, "end": v(-17.55, -60.68) * mm});
            skLineSegment(sketch, "E656", {"start": v(-17.05, -60.68) * mm, "end": v(-14.88, -62.84) * mm});
            skLineSegment(sketch, "E657", {"start": v(-14.88, -62.84) * mm, "end": v(-14.88, -64.41) * mm});
            skLineSegment(sketch, "E658", {"start": v(-14.88, -64.41) * mm, "end": v(-15.1, -64.62) * mm});
            skLineSegment(sketch, "E659", {"start": v(-15.1, -64.62) * mm, "end": v(-19.5, -64.62) * mm});
            skLineSegment(sketch, "E660", {"start": v(-19.5, -64.62) * mm, "end": v(-19.5, -65.68) * mm});
            skLineSegment(sketch, "E661", {"start": v(-22.95, -60.68) * mm, "end": v(-22.45, -60.68) * mm});
            skPoint(sketch, "E662.orphan", {"position": v(-22.7, -60.43) * mm});
            skPoint(sketch, "E663.orphan", {"position": v(-17.3, -60.43) * mm});
            skLineSegment(sketch, "E664.trimOffspring", {"start": v(-17.55, -60.68) * mm, "end": v(-17.05, -60.68) * mm});
            skLineSegment(sketch, "E665.0", {"start": v(-42.62, -75.12) * mm, "end": v(-42.62, -70.12) * mm, "construction": true});
            skLineSegment(sketch, "E666", {"start": v(-145.57, -65.22) * mm, "end": v(-155.1, -65.22) * mm, "construction": true});
            skLineSegment(sketch, "E667.0", {"start": v(-155.1, -65.22) * mm, "end": v(-155.1, -58.08) * mm, "construction": true});
            skLineSegment(sketch, "E668", {"start": v(-42.62, -72.62) * mm, "end": v(-28.74, -72.62) * mm, "construction": true});
            skPoint(sketch, "E668.endSnap0", {"position": v(-42.62, -72.62) * mm});
            skLineSegment(sketch, "E669", {"start": v(-20, -65.68) * mm, "end": v(-20, -63.25) * mm, "construction": true});
            skSolve(sketch);
        }
        {
            var Q0;
            Q0 = qSketchRegion(id + "F6", true);
            var Q1;
            Q1=sQuery(id+"F6.wireOp",EDGE,"E649");
            revolve(context, id + "F7", {"entities" : qUnion([Q0]), "axis" : qUnion([Q1]), "revolveType" : RevolveType.FULL});
        }
        {
            var Q0;
            Q0=makeQuery(id+"F5.opRevolve","SWEPT_FACE",FACE,{"disambiguationData":[OSD([sQuery(id+"F4.wireOp",EDGE,"E631.MirrorCS")])]});
            cPlane(context, id + "F8", {"entities" : qUnion([Q0]), "cplaneType" : CPlaneType.OFFSET, "offset" : 7.4 * mm, "width" : 150 * mm, "height" : 150 * mm});
        }
        {
            var Q0;
            Q0=qCreatedBy(id+"F8.planeOp",FACE);
            var sketch = newSketch(context, id + "F9", { "sketchPlane" : qUnion([Q0])});
            skLineSegment(sketch, "E670", {"start": v(200, 364.18) * mm, "end": v(200, -72.62) * mm, "construction": true});
            skLineSegment(sketch, "E671", {"start": v(200, -72.62) * mm, "end": v(400, -72.62) * mm, "construction": true});
            skLineSegment(sketch, "E672", {"start": v(200, -72.62) * mm, "end": v(0, -72.62) * mm, "construction": true});
            skCircle(sketch, "E673", {"center": v(0, -72.62) * mm, "radius": 3.57 * mm});
            skCircle(sketch, "E674", {"center": v(400, -72.62) * mm, "radius": 3.57 * mm});
            skLineSegment(sketch, "E675", {"start": v(0, 72.62) * mm, "end": v(40, 72.62) * mm, "construction": true});
            skLineSegment(sketch, "E676", {"start": v(40, 72.62) * mm, "end": v(200, 72.62) * mm, "construction": true});
            skLineSegment(sketch, "E677", {"start": v(200, 72.62) * mm, "end": v(360, 72.62) * mm, "construction": true});
            skLineSegment(sketch, "E678", {"start": v(360, 72.62) * mm, "end": v(400, 72.62) * mm, "construction": true});
            skCircle(sketch, "E679", {"center": v(0, 72.62) * mm, "radius": 2.5 * mm});
            skCircle(sketch, "E680", {"center": v(40, 72.62) * mm, "radius": 2.5 * mm});
            skCircle(sketch, "E681", {"center": v(360, 72.62) * mm, "radius": 2.5 * mm});
            skCircle(sketch, "E682", {"center": v(400, 72.62) * mm, "radius": 2.5 * mm});
            skLineSegment(sketch, "E683", {"start": v(0, 72.62) * mm, "end": v(0, -72.62) * mm, "construction": true});
            skLineSegment(sketch, "E684", {"start": v(400, 72.62) * mm, "end": v(400, -72.62) * mm, "construction": true});
            skCircle(sketch, "E685", {"center": v(40, -72.62) * mm, "radius": 3.57 * mm});
            skCircle(sketch, "E686.MirrorC", {"center": v(360, -72.62) * mm, "radius": 3.57 * mm});
            skLineSegment(sketch, "E687", {"start": v(0.67, 84.65) * mm, "end": v(110, 84.65) * mm});
            skLineSegment(sketch, "E688", {"start": v(-12.03, 71.95) * mm, "end": v(-12.02, -73.01) * mm});
            skLineSegment(sketch, "E689", {"start": v(0.68, -85.71) * mm, "end": v(200, -85.71) * mm});
            skPoint(sketch, "E690.visualSharp", {"position": v(-12.03, 84.65) * mm});
            skArc(sketch, "E690.filletArc", {"start": v(0.68, 84.65) * mm, "mid": v(-8.3, 80.93) * mm, "end": v(-12.03, 71.95) * mm});
            skPoint(sketch, "E691.visualSharp", {"position": v(-12.02, -85.71) * mm});
            skArc(sketch, "E691.filletArc", {"start": v(-12.02, -73.01) * mm, "mid": v(-8.3, -82) * mm, "end": v(0.68, -85.71) * mm});
            skLineSegment(sketch, "E692", {"start": v(160, 134.65) * mm, "end": v(160, 155.12) * mm});
            skLineSegment(sketch, "E693", {"start": v(169.53, 164.65) * mm, "end": v(200, 164.65) * mm});
            skPoint(sketch, "E694.visualSharp", {"position": v(160, 84.65) * mm});
            skArc(sketch, "E694.filletArc", {"start": v(110, 84.65) * mm, "mid": v(145.36, 99.3) * mm, "end": v(160, 134.65) * mm});
            skPoint(sketch, "E695.visualSharp", {"position": v(160, 164.65) * mm});
            skArc(sketch, "E695.filletArc", {"start": v(169.53, 164.65) * mm, "mid": v(162.79, 161.86) * mm, "end": v(160, 155.12) * mm});
            skLineSegment(sketch, "E696.0", {"start": v(190, 364.18) * mm, "end": v(190, 98.32) * mm, "construction": true});
            skLineSegment(sketch, "E697.0", {"start": v(170, 364.18) * mm, "end": v(170, 98.32) * mm, "construction": true});
            skLineSegment(sketch, "E698", {"start": v(110, 84.65) * mm, "end": v(200, 84.65) * mm, "construction": true});
            skLineSegment(sketch, "E699.0", {"start": v(121.9, 94.65) * mm, "end": v(200, 94.65) * mm, "construction": true});
            skCircle(sketch, "E700", {"center": v(170, 94.65) * mm, "radius": 2.52 * mm});
            skCircle(sketch, "E701.0.1.0", {"center": v(170, 114.65) * mm, "radius": 2.52 * mm});
            skCircle(sketch, "E701.0.2.0", {"center": v(170, 134.65) * mm, "radius": 2.52 * mm});
            skCircle(sketch, "E701.0.3.0", {"center": v(170, 154.65) * mm, "radius": 2.52 * mm});
            skCircle(sketch, "E701.1.0.0", {"center": v(190, 94.65) * mm, "radius": 2.52 * mm});
            skCircle(sketch, "E701.1.1.0", {"center": v(190, 114.65) * mm, "radius": 2.52 * mm});
            skCircle(sketch, "E701.1.2.0", {"center": v(190, 134.65) * mm, "radius": 2.52 * mm});
            skCircle(sketch, "E701.1.3.0", {"center": v(190, 154.65) * mm, "radius": 2.52 * mm});
            skLineSegment(sketch, "E701.direction1", {"start": v(170, 94.65) * mm, "end": v(190, 94.65) * mm, "construction": true});
            skLineSegment(sketch, "E701.direction2", {"start": v(170, 94.65) * mm, "end": v(170, 114.65) * mm, "construction": true});
            skLineSegment(sketch, "E702.MirrorCS", {"start": v(230.47, 164.65) * mm, "end": v(200, 164.65) * mm});
            skArc(sketch, "E703.MirrorCS", {"start": v(230.48, 164.65) * mm, "mid": v(237.21, 161.86) * mm, "end": v(240, 155.12) * mm});
            skLineSegment(sketch, "E704.MirrorCS", {"start": v(240, 134.65) * mm, "end": v(240, 155.12) * mm});
            skArc(sketch, "E705.MirrorCS", {"start": v(290, 84.65) * mm, "mid": v(254.64, 99.3) * mm, "end": v(240, 134.65) * mm});
            skLineSegment(sketch, "E706.MirrorCS", {"start": v(399.32, 84.65) * mm, "end": v(290, 84.65) * mm});
            skArc(sketch, "E707.MirrorCS", {"start": v(399.32, 84.65) * mm, "mid": v(408.3, 80.93) * mm, "end": v(412.02, 71.95) * mm});
            skLineSegment(sketch, "E708.MirrorCS", {"start": v(412.03, 71.95) * mm, "end": v(412.03, -73.01) * mm});
            skArc(sketch, "E709.MirrorCS", {"start": v(412.03, -73.01) * mm, "mid": v(408.3, -82) * mm, "end": v(399.33, -85.71) * mm});
            skLineSegment(sketch, "E710.MirrorCS", {"start": v(399.33, -85.71) * mm, "end": v(200, -85.71) * mm});
            skCircle(sketch, "E711.MirrorC", {"center": v(210, 154.65) * mm, "radius": 2.52 * mm});
            skCircle(sketch, "E712.MirrorC", {"center": v(230, 154.65) * mm, "radius": 2.52 * mm});
            skCircle(sketch, "E713.MirrorC", {"center": v(230, 134.65) * mm, "radius": 2.52 * mm});
            skCircle(sketch, "E714.MirrorC", {"center": v(210, 134.65) * mm, "radius": 2.52 * mm});
            skCircle(sketch, "E715.MirrorC", {"center": v(210, 114.65) * mm, "radius": 2.52 * mm});
            skCircle(sketch, "E716.MirrorC", {"center": v(210, 94.65) * mm, "radius": 2.52 * mm});
            skCircle(sketch, "E717.MirrorC", {"center": v(230, 94.65) * mm, "radius": 2.52 * mm});
            skCircle(sketch, "E718.MirrorC", {"center": v(230, 114.65) * mm, "radius": 2.52 * mm});
            skCircle(sketch, "E719.0", {"center": v(0, 72.62) * mm, "radius": 6.95 * mm, "construction": true});
            skCircle(sketch, "E720.0", {"center": v(0, -72.62) * mm, "radius": 6.95 * mm, "construction": true});
            skSolve(sketch);
        }
        {
            var Q0;
            Q0 = qSketchRegion(id + "F9", true);
            extrude(context, id + "F10", {"entities" : qUnion([Q0]), "depth" : 9.52 * mm});
        }
    });
